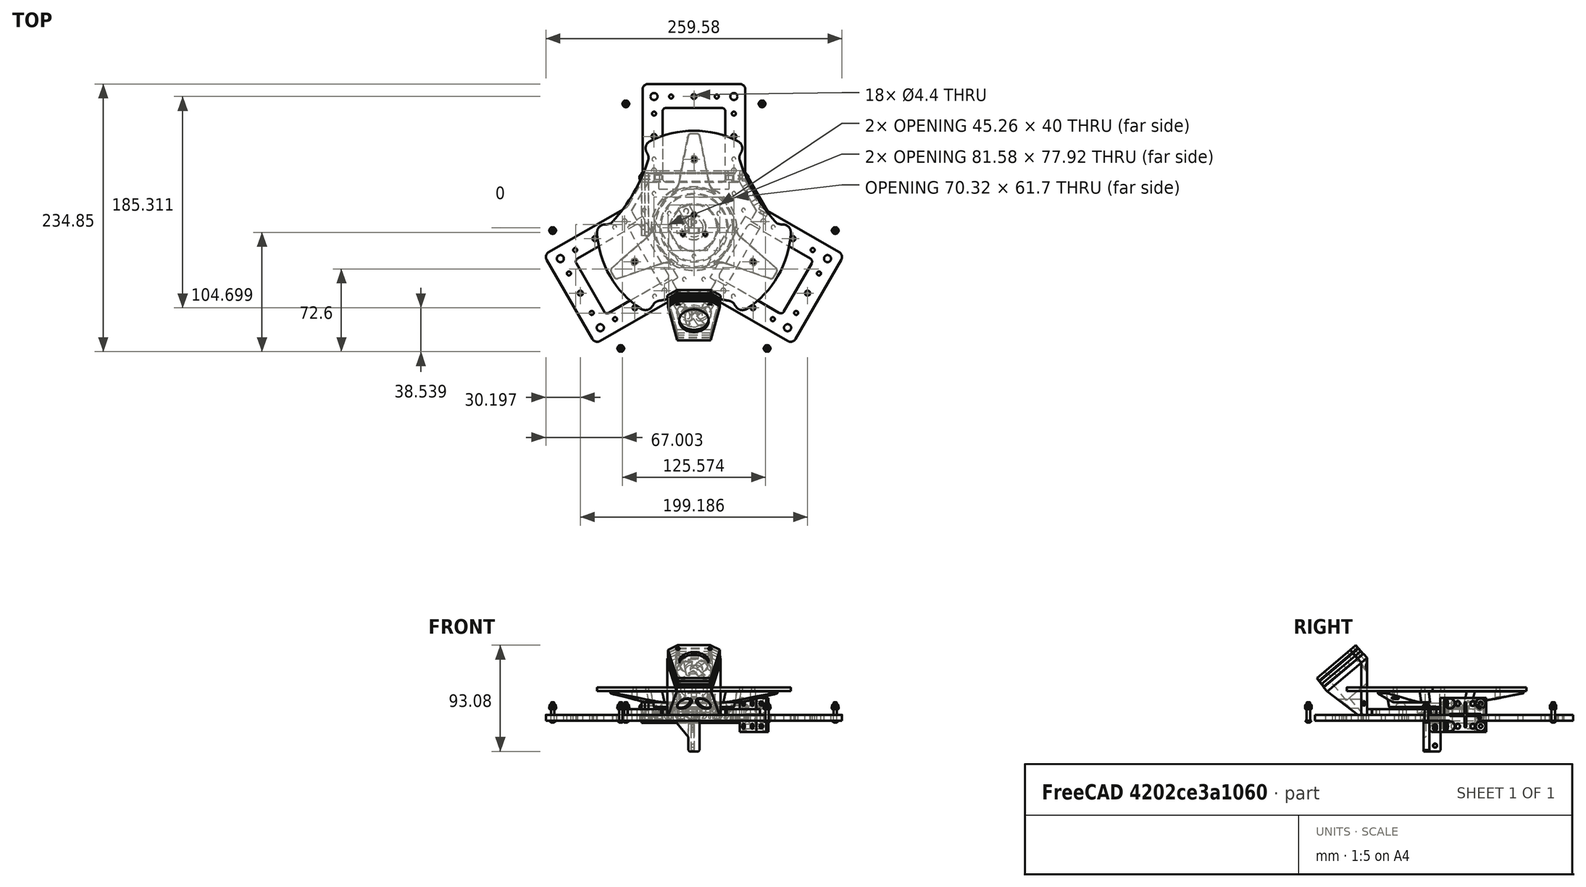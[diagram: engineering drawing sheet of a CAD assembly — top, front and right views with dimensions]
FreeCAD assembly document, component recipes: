
FREECAD ASSEMBLY — COMPONENT RECIPES ("structures")

This assembly document has 14 components, labeled P0..P13 below (a component is one placed body or linked part). 12 of them carry a construction recipe — the FreeCAD feature program that regenerates the part from scratch, quoted from this document or its linked companion documents; the rest are supplied as boundary geometry only. No exploded tour is included for this assembly.
NOTE — this tour is split across 2 documents so each fits a 32k-token context. This is document 1: the component sections continue in the remaining 1 document, each repeating the header above.
COMPONENT P0 — recipe-attached ("PlaqueIntermediaire", modeled in this document).
Construction recipe (the document's own serialized feature program — sketch geometry with constraints, then the solid features built on it; lengths are millimeters unless a unit is written):

FEATURE [Sketcher::SketchObject] Sketch043
  ArcFitTolerance = 0
  AttachmentSupport = -> [XY_Plane031]
  ExternalBSplineMaxDegree = 0
  ExternalBSplineTolerance = 0
  FullyConstrained = true
  InternalTolerance = 1e-06
  InvalidShape = false
  MakeInternals = false
  MapMode = 5
  Support = -> [XY_Plane031]
  TreeRank = 0
  ValidateShape = true
  sketch-geometry (13):
    g0: LineSegment StartX=0 StartY=0 StartZ=0 EndX=0 EndY=-54.641 EndZ=0
    g1: LineSegment StartX=0 StartY=-54.641 StartZ=0 EndX=-14.641 EndY=-54.641 EndZ=0
    g2: LineSegment StartX=-14.641 StartY=-54.641 StartZ=0 EndX=-19.641 EndY=-45.9808 EndZ=0
    g3: LineSegment StartX=-19.641 StartY=-45.9808 StartZ=0 EndX=-28.3013 EndY=-50.9808 EndZ=0
    g4: LineSegment StartX=-28.3013 StartY=-50.9808 StartZ=0 EndX=-58.3013 EndY=0.980762 EndZ=0
    g5: LineSegment StartX=-58.3013 StartY=0.980762 StartZ=0 EndX=-49.641 EndY=5.98076 EndZ=0
    g6: LineSegment StartX=-49.641 StartY=5.98076 StartZ=0 EndX=-54.641 EndY=14.641 EndZ=0
    g7: LineSegment StartX=-54.641 StartY=14.641 StartZ=0 EndX=-47.3205 EndY=27.3205 EndZ=0
    g8: LineSegment StartX=-47.3205 StartY=27.3205 StartZ=0 EndX=0 EndY=0 EndZ=0
    g9: LineSegment [constr] StartX=-49.641 StartY=5.98076 StartZ=0 EndX=-19.641 EndY=-45.9808 EndZ=0
    g10: Circle CenterX=-43.4808 CenterY=15.3109 CenterZ=0 NormalX=0 NormalY=0 NormalZ=1 AngleXU=0 Radius=1.6
    g11: Circle CenterX=-8.48076 CenterY=-45.3109 CenterZ=0 NormalX=0 NormalY=0 NormalZ=1 AngleXU=0 Radius=1.6
    g12: LineSegment [constr] StartX=0 StartY=0 StartZ=0 EndX=-43.3013 EndY=-25 EndZ=0
  constraints (35):
    c: Coincident(g0,g-1)
    c: PointOnObject(g0,g-2)
    c: Coincident(g1,g0)
    c: Horizontal(g1)
    c: Coincident(g1,g2)
    c: Coincident(g2,g3)
    c: Coincident(g3,g4)
    c: Coincident(g4,g5)
    c: Coincident(g5,g6)
    c: Coincident(g6,g7)
    c: Coincident(g7,g8)
    c: Coincident(g8,g0)
    c: Angle(g8,g0) = 2.0944
    c: Perpendicular(g7,g8)
    c: Perpendicular(g3,g2)
    c: Perpendicular(g4,g3)
    c: Perpendicular(g4,g5)
    c: Perpendicular(g6,g5)
    c: Equal(g7,g1)
    c: Coincident(g9,g5)
    c: Tangent(g9,g2) = 1.5708
    c: Equal(g2,g3)
    c: Equal(g5,g6)
    c: Distance(g6) = 10
    c: Equal(g0,g8)
    c: Distance(g4) = 60
    c: Distance(g0,g9) = 40
    c: Coincident(g12,g0)
    c: PointOnObject(g12,g4)
    c: Perpendicular(g4,g12)
    c: Symmetric(g11,g10,g12)
    c: Diameter(g10) = 3.2
    c: Equal(g10,g11)
    c: Distance(g11,g2) = 10
    c: Distance(g11,g12) = 35
FEATURE [PartDesign::Pad] Pad027
  AddSubType = 0
  AutoTaperInnerAngle = false
  CheckUpToFaceLimits = true
  ClaimChildren = false
  Direction = (1,1,1)
  Fit = 0
  FitJoin = 0
  InnerFit = 0
  InnerFitJoin = 0
  InvalidShape = false
  Length = 5
  Length2 = 100
  Linearize = true
  NewSolid = false
  Profile = -> Sketch043
  Refine = true
  Suppress = false
  TaperInnerAngle = 0
  TaperInnerAngleRev = 0
  TreeRank = 0
  Type = 0
  ValidateShape = true
  _ProfileBasedVersion = 1
FEATURE [PartDesign::PolarPattern] PolarPattern014
  AddSubType = 0
  Angle = 360
  Axis = -> Sketch043 [N_Axis]
  BaseFeature = -> Pad027
  CopyShape = false
  InvalidShape = false
  NewSolid = false
  Occurrences = 3
  OriginalSubs = -> [Pad027]
  Originals = -> [Pad027]
  ParallelTransform = true
  Refine = true
  SubTransform = true
  Suppress = false
  TreeRank = 0
  ValidateShape = true
  _Version = 2
FEATURE [Sketcher::SketchObject] Sketch044
  ArcFitTolerance = 0
  AttachmentSupport = -> [XY_Plane031]
  ExternalBSplineMaxDegree = 0
  ExternalBSplineTolerance = 0
  FullyConstrained = true
  InternalTolerance = 1e-06
  InvalidShape = false
  MakeInternals = false
  MapMode = 5
  Support = -> [XY_Plane031]
  TreeRank = 0
  ValidateShape = true
  sketch-geometry (5):
    g0: LineSegment StartX=-35.6218 StartY=8.30127 StartZ=0 EndX=-10.6218 EndY=-35 EndZ=0
    g1: LineSegment StartX=-10.6218 StartY=-35 StartZ=0 EndX=0 EndY=-35 EndZ=0
    g2: LineSegment StartX=0 StartY=-35 StartZ=0 EndX=0 EndY=0 EndZ=0
    g3: LineSegment StartX=0 StartY=0 StartZ=0 EndX=-30.3109 EndY=17.5 EndZ=0
    g4: LineSegment StartX=-30.3109 StartY=17.5 StartZ=0 EndX=-35.6218 EndY=8.30127 EndZ=0
  constraints (14):
    c: Coincident(g0,g1)
    c: PointOnObject(g1,g-2)
    c: Horizontal(g1)
    c: Coincident(g1,g2)
    c: Coincident(g2,g-1)
    c: Coincident(g2,g3)
    c: Coincident(g3,g4)
    c: Coincident(g4,g0)
    c: Perpendicular(g4,g3)
    c: Equal(g4,g1)
    c: Equal(g2,g3)
    c: Angle(g3,g2) = 2.0944
    c: Distance(g0) = 50
    c: DistanceY(g2,g2) = 35
FEATURE [PartDesign::Pocket] Pocket017
  AddSubType = 1
  AutoTaperInnerAngle = false
  BaseFeature = -> PolarPattern014
  CheckUpToFaceLimits = true
  ClaimChildren = false
  Fit = 0
  FitJoin = 0
  InnerFit = 0
  InnerFitJoin = 0
  InvalidShape = false
  Length = 5
  Length2 = 100
  Linearize = true
  NewSolid = false
  Profile = -> Sketch044
  Refine = true
  Reversed = true
  Suppress = false
  TaperInnerAngle = 0
  TaperInnerAngleRev = 0
  TreeRank = 0
  Type = 1
  ValidateShape = true
  _ProfileBasedVersion = 1
  _Version = 0
FEATURE [PartDesign::PolarPattern] PolarPattern015
  AddSubType = 0
  Angle = 360
  Axis = -> Sketch044 [N_Axis]
  BaseFeature = -> Pocket017
  CopyShape = false
  InvalidShape = false
  NewSolid = false
  Occurrences = 3
  OriginalSubs = -> [Pocket017]
  Originals = -> [Pocket017]
  ParallelTransform = true
  Refine = true
  SubTransform = true
  Suppress = false
  TreeRank = 0
  ValidateShape = true
  _Version = 2
FEATURE [PartDesign::Chamfer] Chamfer007
  AddSubType = 0
  Angle = 45
  Base = -> PolarPattern015 [Edge8,Edge66,Edge67,Edge68,Edge77,Edge78]
  BaseFeature = -> PolarPattern015
  ChamferType = 0
  FlipDirection = false
  InvalidShape = false
  NewSolid = false
  Refine = true
  Size = 1
  Size2 = 1
  SupportTransform = false
  Suppress = false
  TreeRank = 0
  ValidateShape = true
FEATURE [PartDesign::Fillet] Fillet014
  AddSubType = 0
  Base = -> Chamfer007 [Edge101,Edge103,Edge104,Edge105,Edge106,Edge102]
  BaseFeature = -> Chamfer007
  InvalidShape = false
  NewSolid = false
  Radius = 3
  Refine = true
  SupportTransform = false
  Suppress = false
  TreeRank = 0
  ValidateShape = true
FEATURE [PartDesign::Body] Body024  label="PlaqueIntermediaire"
  AutoGroupSolids = false
  ClaimAllChildren = false
  ExportMode = 0
  Group = -> [Sketch043,Pad027,PolarPattern014,Sketch044,Pocket017,PolarPattern015,Chamfer007,Fillet014]
  InvalidShape = false
  Origin = -> Origin036
  SingleSolid = true
  Tip = -> Fillet014
  TreeRank = 0
  ValidateShape = true
  _ExportChildren = -> [Pad027,PolarPattern014,Pocket017,PolarPattern015,Chamfer007,Fillet014]
  _GroupVersion = 1
COMPONENT P1 — recipe-attached ("CoinStandard", modeled in this document).
Construction recipe (the document's own serialized feature program — sketch geometry with constraints, then the solid features built on it; lengths are millimeters unless a unit is written):

FEATURE [Sketcher::SketchObject] Sketch060
  ArcFitTolerance = 0
  AttachmentSupport = -> [XY_Plane037]
  ExternalBSplineMaxDegree = 0
  ExternalBSplineTolerance = 0
  FullyConstrained = true
  InternalTolerance = 1e-06
  InvalidShape = false
  MakeInternals = false
  MapMode = 5
  Support = -> [XY_Plane037]
  TreeRank = 0
  ValidateShape = true
  sketch-geometry (10):
    g0: LineSegment [constr] StartX=0 StartY=0 StartZ=0 EndX=34.641 EndY=-20 EndZ=0
    g1: LineSegment [constr] StartX=0 StartY=0 StartZ=0 EndX=-34.641 EndY=-20 EndZ=0
    g2: LineSegment [constr] StartX=-34.641 StartY=-20 StartZ=0 EndX=-14.641 EndY=-54.641 EndZ=0
    g3: LineSegment [constr] StartX=34.641 StartY=-20 StartZ=0 EndX=14.641 EndY=-54.641 EndZ=0
    g4: LineSegment StartX=-14.641 StartY=-54.641 StartZ=0 EndX=-23.3013 EndY=-59.641 EndZ=0
    g5: LineSegment StartX=14.641 StartY=-54.641 StartZ=0 EndX=23.3013 EndY=-59.641 EndZ=0
    g6: LineSegment StartX=-23.3013 StartY=-59.641 StartZ=0 EndX=-15 EndY=-89.641 EndZ=0
    g7: LineSegment StartX=23.3013 StartY=-59.641 StartZ=0 EndX=15 EndY=-89.641 EndZ=0
    g8: LineSegment StartX=-14.641 StartY=-54.641 StartZ=0 EndX=14.641 EndY=-54.641 EndZ=0
    g9: LineSegment StartX=-15 StartY=-89.641 StartZ=0 EndX=15 EndY=-89.641 EndZ=0
  constraints (24):
    c: Coincident(g0,g-1)
    c: Coincident(g1,g0)
    c: Symmetric(g0,g1,g-2)
    c: Angle(g1,g0) = 2.0944
    c: Coincident(g2,g1)
    c: Perpendicular(g1,g2)
    c: Coincident(g3,g0)
    c: Symmetric(g3,g2,g-2)
    c: Distance(g2) = 40
    c: Distance(g0) = 40
    c: Coincident(g4,g2)
    c: Coincident(g5,g3)
    c: Perpendicular(g3,g5)
    c: Symmetric(g4,g5,g-2)
    c: Distance(g5) = 10
    c: Coincident(g6,g4)
    c: Coincident(g7,g5)
    c: Symmetric(g7,g6,g-2)
    c: DistanceY(g7,g3) = 35
    c: Coincident(g8,g4)
    c: Coincident(g8,g5)
    c: Coincident(g9,g6)
    c: Coincident(g9,g7)
    c: DistanceX(g9,g9) = 30
FEATURE [PartDesign::Pad] Pad034
  AddSubType = 0
  AutoTaperInnerAngle = false
  CheckUpToFaceLimits = true
  ClaimChildren = false
  Direction = (1,1,1)
  Fit = 0
  FitJoin = 0
  InnerFit = 0
  InnerFitJoin = 0
  InvalidShape = false
  Length = 50
  Length2 = 100
  Linearize = true
  NewSolid = false
  Profile = -> Sketch060
  Refine = true
  Suppress = false
  TaperInnerAngle = 0
  TaperInnerAngleRev = 0
  TreeRank = 0
  Type = 0
  ValidateShape = true
  _ProfileBasedVersion = 1
FEATURE [Sketcher::SketchObject] Sketch061
  ArcFitTolerance = 0
  AttachmentSupport = -> [YZ_Plane037]
  ExternalBSplineMaxDegree = 0
  ExternalBSplineTolerance = 0
  ExternalGeometry = -> [Pad034]
  FullyConstrained = true
  InternalTolerance = 1e-06
  InvalidShape = false
  MakeInternals = false
  MapMode = 5
  Placement = pos=(0,0,0) rot=(0.57735,0.57735,0.57735;2.0944rad)
  Support = -> [YZ_Plane037]
  TreeRank = 0
  ValidateShape = true
  sketch-geometry (4):
    g0: LineSegment StartX=-62.641 StartY=0 StartZ=0 EndX=-89.641 EndY=20.6315 EndZ=0
    g1: LineSegment StartX=-62.641 StartY=0 StartZ=0 EndX=-89.641 EndY=0 EndZ=0
    g2: LineSegment StartX=-89.641 StartY=0 StartZ=0 EndX=-89.641 EndY=20.6315 EndZ=0
    g3: LineSegment [constr] StartX=-89.641 StartY=20.6315 StartZ=0 EndX=-54.641 EndY=50 EndZ=0
  constraints (11):
    c: PointOnObject(g0,g-4)
    c: PointOnObject(g0,g-1)
    c: DistanceX(g0,g-3) = 3
    c: Coincident(g0,g1)
    c: PointOnObject(g1,g-4)
    c: Horizontal(g1)
    c: Coincident(g1,g2)
    c: Coincident(g2,g0)
    c: Coincident(g3,g0)
    c: Coincident(g3,g-5)
    c: Angle(g-4,g3) = 2.26893
FEATURE [PartDesign::Pocket] Pocket025
  AddSubType = 1
  AutoTaperInnerAngle = false
  BaseFeature = -> Pad034
  CheckUpToFaceLimits = true
  ClaimChildren = false
  Fit = 0
  FitJoin = 0
  InnerFit = 0
  InnerFitJoin = 0
  InvalidShape = false
  Length = 5
  Length2 = 100
  Linearize = true
  Midplane = true
  NewSolid = false
  Profile = -> Sketch061
  Refine = true
  Suppress = false
  TaperInnerAngle = 0
  TaperInnerAngleRev = 0
  TreeRank = 0
  Type = 1
  ValidateShape = true
  _ProfileBasedVersion = 1
  _Version = 1
FEATURE [Sketcher::SketchObject] Sketch062
  ArcFitTolerance = 0
  AttachmentSupport = -> [YZ_Plane037]
  ExternalBSplineMaxDegree = 0
  ExternalBSplineTolerance = 0
  ExternalGeometry = -> [Pocket025]
  FullyConstrained = true
  InternalTolerance = 1e-06
  InvalidShape = false
  MakeInternals = false
  MapMode = 5
  Placement = pos=(0,0,0) rot=(0.57735,0.57735,0.57735;2.0944rad)
  Support = -> [YZ_Plane037]
  TreeRank = 0
  ValidateShape = true
  sketch-geometry (3):
    g0: LineSegment StartX=-89.641 StartY=50 StartZ=0 EndX=-89.641 EndY=20.6315 EndZ=0
    g1: LineSegment StartX=-89.641 StartY=20.6315 StartZ=0 EndX=-54.641 EndY=50 EndZ=0
    g2: LineSegment StartX=-89.641 StartY=50 StartZ=0 EndX=-54.641 EndY=50 EndZ=0
  constraints (6):
    c: Coincident(g1,g0)
    c: Coincident(g-3,g0)
    c: Coincident(g-3,g0)
    c: Coincident(g2,g0)
    c: Coincident(g2,g1)
    c: Coincident(g1,g-5)
FEATURE [PartDesign::Pocket] Pocket026
  AddSubType = 1
  AutoTaperInnerAngle = false
  BaseFeature = -> Pocket025
  CheckUpToFaceLimits = true
  ClaimChildren = false
  Fit = 0
  FitJoin = 0
  InnerFit = 0
  InnerFitJoin = 0
  InvalidShape = false
  Length = 5
  Length2 = 100
  Linearize = true
  Midplane = true
  NewSolid = false
  Profile = -> Sketch062
  Refine = true
  Suppress = false
  TaperInnerAngle = 0
  TaperInnerAngleRev = 0
  TreeRank = 0
  Type = 1
  ValidateShape = true
  _ProfileBasedVersion = 1
  _Version = 1
FEATURE [PartDesign::Plane] DatumPlane
  AttachmentOffset = pos=(0,0,-30) rot=(0,0,1;0rad)
  AttachmentSupport = -> [Pocket026]
  InvalidShape = false
  Length = 67.9904
  MapMode = 5
  MinimumLength = 10
  MinimumWidth = 10
  Placement = pos=(-35,-60.6218,3.3e-15) rot=(0.186157,0.694747,0.694747;2.77349rad)
  ResizeMode = 0
  Support = -> [Pocket026]
  TreeRank = 0
  ValidateShape = true
  Width = 50
FEATURE [Sketcher::SketchObject] Sketch063
  ArcFitTolerance = 0
  AttachmentSupport = -> [DatumPlane]
  ExternalBSplineMaxDegree = 0
  ExternalBSplineTolerance = 0
  ExternalGeometry = -> [Pocket026]
  FullyConstrained = true
  InternalTolerance = 1e-06
  InvalidShape = false
  MakeInternals = false
  MapMode = 5
  Placement = pos=(-35,-60.6218,3.3e-15) rot=(0.186157,0.694747,0.694747;2.77349rad)
  Support = -> [DatumPlane]
  TreeRank = 0
  ValidateShape = true
  sketch-geometry (2):
    g0: Circle CenterX=-45 CenterY=10 CenterZ=0 NormalX=0 NormalY=0 NormalZ=1 AngleXU=0 Radius=1.6
    g1: LineSegment [constr] StartX=-50 StartY=10 StartZ=0 EndX=-40 EndY=10 EndZ=0
  constraints (6):
    c: PointOnObject(g1,g-3)
    c: PointOnObject(g1,g-4)
    c: Horizontal(g1)
    c: Symmetric(g1,g1,g0)
    c: Diameter(g0) = 3.2
    c: Distance(g-3,g1) = 10
FEATURE [PartDesign::Hole] Hole001
  AddSubType = 1
  BaseFeature = -> Pocket026
  ClaimChildren = false
  CustomThreadClearance = 0
  Depth = 39
  DepthType = 0
  Diameter = 3.2
  DrillForDepth = false
  DrillPoint = 1
  DrillPointAngle = 118
  Fit = 0
  FitJoin = 0
  HoleCutCountersinkAngle = 90
  HoleCutCustomValues = true
  HoleCutDepth = 27
  HoleCutDiameter = 8
  HoleCutType = 1
  InnerFit = 0
  InnerFitJoin = 0
  InvalidShape = false
  ModelThread = false
  NewSolid = false
  Profile = -> Sketch063
  Refine = true
  Reversed = true
  Suppress = false
  Tapered = false
  TaperedAngle = 90
  ThreadClass = 0
  ThreadDepth = 39
  ThreadDepthType = 0
  ThreadDirection = 0
  ThreadFit = 0
  ThreadSize = 0
  ThreadType = 0
  Threaded = false
  TreeRank = 0
  UseCustomThreadClearance = false
  ValidateShape = true
  _ProfileBasedVersion = 1
FEATURE [PartDesign::Mirrored] Mirrored006
  AddSubType = 0
  BaseFeature = -> Hole001
  CopyShape = false
  InvalidShape = false
  MirrorPlane = -> YZ_Plane037
  NewSolid = false
  OriginalSubs = -> [Hole001]
  Originals = -> [Hole001]
  ParallelTransform = true
  Refine = true
  SubTransform = true
  Suppress = false
  TreeRank = 0
  ValidateShape = true
  _Version = 3
FEATURE [Sketcher::SketchObject] Sketch064
  ArcFitTolerance = 0
  AttachmentSupport = -> [Mirrored006]
  ExternalBSplineMaxDegree = 0
  ExternalBSplineTolerance = 0
  ExternalGeometry = -> [Mirrored006]
  FullyConstrained = true
  InternalTolerance = 1e-06
  InvalidShape = false
  MakeInternals = false
  MapMode = 5
  Placement = pos=(-2.64e-14,-47.1965,56.2467) rot=(1,0,0;0.698132rad)
  Support = -> [Mirrored006]
  TreeRank = 0
  ValidateShape = true
  sketch-geometry (2):
    g0: Circle CenterX=-14 CenterY=-14.7181 CenterZ=0 NormalX=0 NormalY=0 NormalZ=1 AngleXU=0 Radius=2.05
    g1: Circle CenterX=14 CenterY=-14.7181 CenterZ=0 NormalX=0 NormalY=0 NormalZ=1 AngleXU=0 Radius=2.05
  constraints (5):
    c: Symmetric(g1,g0,g-2)
    c: Diameter(g0) = 4.1
    c: Equal(g0,g1)
    c: DistanceX(g0,g1) = 28
    c: DistanceY(g0,g-3) = 5
FEATURE [PartDesign::Pocket] Pocket027
  AddSubType = 1
  AutoTaperInnerAngle = false
  BaseFeature = -> Mirrored006
  CheckUpToFaceLimits = true
  ClaimChildren = false
  Fit = 0
  FitJoin = 0
  InnerFit = 0
  InnerFitJoin = 0
  InvalidShape = false
  Length = 5
  Length2 = 100
  Linearize = true
  NewSolid = false
  Profile = -> Sketch064
  Refine = true
  Suppress = false
  TaperInnerAngle = 0
  TaperInnerAngleRev = 0
  TreeRank = 0
  Type = 1
  ValidateShape = true
  _ProfileBasedVersion = 1
  _Version = 1
FEATURE [Sketcher::SketchObject] Sketch065
  ArcFitTolerance = 0
  AttachmentSupport = -> [Pocket027]
  ExternalBSplineMaxDegree = 0
  ExternalBSplineTolerance = 0
  ExternalGeometry = -> [Pocket027]
  FullyConstrained = true
  InternalTolerance = 1e-06
  InvalidShape = false
  MakeInternals = false
  MapMode = 5
  Placement = pos=(-2.64e-14,-47.1965,56.2467) rot=(1,0,0;0.698132rad)
  Support = -> [Pocket027]
  TreeRank = 0
  ValidateShape = true
  sketch-geometry (3):
    g0: Circle CenterX=0 CenterY=-32.5627 CenterZ=0 NormalX=0 NormalY=0 NormalZ=1 AngleXU=0 Radius=15
    g1: GeomPoint [constr] X=2e-16 Y=-55.4073 Z=0
    g2: GeomPoint [constr] X=0 Y=-9.71807 Z=0
  constraints (6):
    c: PointOnObject(g0,g-2)
    c: Diameter(g0) = 30
    c: PointOnObject(g2,g-2)
    c: PointOnObject(g2,g-3)
    c: PointOnObject(g1,g-4)
    c: Symmetric(g1,g2,g0)
FEATURE [PartDesign::Pocket] Pocket028
  AddSubType = 1
  AutoTaperInnerAngle = false
  BaseFeature = -> Pocket027
  CheckUpToFaceLimits = true
  ClaimChildren = false
  Fit = 0
  FitJoin = 0
  InnerFit = 0
  InnerFitJoin = 0
  InvalidShape = false
  Length = 17
  Length2 = 100
  Linearize = true
  NewSolid = false
  Profile = -> Sketch065
  Refine = true
  Suppress = false
  TaperInnerAngle = 0
  TaperInnerAngleRev = 0
  TreeRank = 0
  Type = 0
  ValidateShape = true
  _ProfileBasedVersion = 1
  _Version = 1
FEATURE [Sketcher::SketchObject] Sketch066
  ArcFitTolerance = 0
  AttachmentSupport = -> [Pocket028]
  ExternalBSplineMaxDegree = 0
  ExternalBSplineTolerance = 0
  ExternalGeometry = -> [Pocket028]
  FullyConstrained = true
  InternalTolerance = 1e-06
  InvalidShape = false
  MakeInternals = false
  MapMode = 5
  Placement = pos=(-2.64e-14,-47.1965,56.2467) rot=(1,0,0;0.698132rad)
  Support = -> [Pocket028]
  TreeRank = 0
  ValidateShape = true
  sketch-geometry (4):
    g0: ArcOfCircle CenterX=0 CenterY=-32.5627 CenterZ=0 NormalX=0 NormalY=0 NormalZ=1 AngleXU=0 Radius=11.5 StartAngle=3.22982 EndAngle=6.19496
    g1: LineSegment StartX=-11.4553 StartY=-33.576 StartZ=0 EndX=-12.3039 EndY=-23.9828 EndZ=0
    g2: LineSegment StartX=12.3039 StartY=-23.9828 StartZ=0 EndX=11.4553 EndY=-33.576 EndZ=0
    g3: LineSegment StartX=-12.3039 StartY=-23.9828 StartZ=0 EndX=12.3039 EndY=-23.9828 EndZ=0
  constraints (8):
    c: Coincident(g0,g-3)
    c: Diameter(g0) = 23
    c: Coincident(g1,g-4)
    c: Coincident(g2,g-4)
    c: Coincident(g3,g1)
    c: Coincident(g3,g2)
    c: Tangent(g1,g0) = 1.5708
    c: Tangent(g2,g0) = 1.5708
FEATURE [PartDesign::Pocket] Pocket029
  AddSubType = 1
  AutoTaperInnerAngle = false
  BaseFeature = -> Pocket028
  CheckUpToFaceLimits = true
  ClaimChildren = false
  Fit = 0
  FitJoin = 0
  InnerFit = 0
  InnerFitJoin = 0
  InvalidShape = false
  Length = 5
  Length2 = 100
  Linearize = true
  NewSolid = false
  Profile = -> Sketch066
  Refine = true
  Suppress = false
  TaperInnerAngle = 0
  TaperInnerAngleRev = 0
  TreeRank = 0
  Type = 1
  ValidateShape = true
  _ProfileBasedVersion = 1
  _Version = 1
FEATURE [PartDesign::Chamfer] Chamfer018
  AddSubType = 0
  Angle = 45
  Base = -> Pocket029 [Edge44,Edge31]
  BaseFeature = -> Pocket029
  ChamferType = 0
  FlipDirection = false
  InvalidShape = false
  NewSolid = false
  Refine = true
  Size = 0.4
  Size2 = 1
  SupportTransform = false
  Suppress = false
  TreeRank = 0
  ValidateShape = true
FEATURE [PartDesign::Pad] Pad036
  AddSubType = 0
  AutoTaperInnerAngle = false
  BaseFeature = -> Chamfer018
  CheckUpToFaceLimits = true
  ClaimChildren = false
  Direction = (1,1,1)
  Fit = 0
  FitJoin = 0
  InnerFit = 0
  InnerFitJoin = 0
  InvalidShape = false
  Length = 5
  Length2 = 100
  Linearize = true
  NewSolid = false
  Profile = -> Chamfer018 [Face5]
  Refine = true
  Suppress = false
  TaperInnerAngle = 0
  TaperInnerAngleRev = 0
  TreeRank = 0
  Type = 0
  ValidateShape = true
  _ProfileBasedVersion = 1
FEATURE [PartDesign::Chamfer] Chamfer022
  AddSubType = 0
  Angle = 45
  Base = -> Pad036 [Face15]
  BaseFeature = -> Pad036
  ChamferType = 0
  FlipDirection = false
  InvalidShape = false
  NewSolid = false
  Refine = true
  Size = 0.4
  Size2 = 1
  SupportTransform = false
  Suppress = false
  TreeRank = 0
  ValidateShape = true
FEATURE [PartDesign::Chamfer] Chamfer023
  AddSubType = 0
  Angle = 45
  Base = -> Chamfer022 [Edge64,Edge63]
  BaseFeature = -> Chamfer022
  ChamferType = 0
  FlipDirection = false
  InvalidShape = false
  NewSolid = false
  Refine = true
  Size = 1
  Size2 = 1
  SupportTransform = false
  Suppress = false
  TreeRank = 0
  ValidateShape = true
FEATURE [PartDesign::Body] Body029  label="CoinStandard"
  AutoGroupSolids = false
  ClaimAllChildren = false
  ExportMode = 0
  Group = -> [Sketch060,Pad034,Sketch061,Pocket025,Sketch062,Pocket026,DatumPlane,Sketch063,Hole001,Mirrored006,Sketch064,Pocket027,Sketch065,Pocket028,Sketch066,Pocket029,Chamfer018,Pad036,Chamfer022,Chamfer023]
  InvalidShape = false
  Origin = -> Origin046
  SingleSolid = true
  Tip = -> Chamfer023
  TreeRank = 0
  ValidateShape = true
  _ExportChildren = -> [Pad034,Pocket025,Pocket026,DatumPlane,Hole001,Mirrored006,Pocket027,Pocket028,Pocket029,Chamfer018,Pad036,Chamfer022,Chamfer023]
  _GroupVersion = 1
COMPONENT P2 — recipe-attached ("Link075(Semelle)", modeled in this document).
Construction recipe (the document's own serialized feature program — sketch geometry with constraints, then the solid features built on it; lengths are millimeters unless a unit is written):

FEATURE [Sketcher::SketchObject] Sketch032
  ArcFitTolerance = 0
  AttachmentSupport = -> [XY_Plane026]
  ExternalBSplineMaxDegree = 0
  ExternalBSplineTolerance = 0
  FullyConstrained = true
  InternalTolerance = 1e-06
  InvalidShape = false
  MakeInternals = false
  MapMode = 5
  Support = -> [XY_Plane026]
  TreeRank = 0
  ValidateShape = true
  sketch-geometry (56):
    g0: LineSegment StartX=-131.619 StartY=-24.0289 StartZ=0 EndX=-58.007 EndY=18.4711 EndZ=0
    g1: LineSegment StartX=-58.007 StartY=18.4711 StartZ=0 EndX=-45 EndY=41 EndZ=0
    g2: LineSegment StartX=-45 StartY=41 StartZ=0 EndX=-45 EndY=126 EndZ=0
    g3: LineSegment StartX=-45 StartY=126 StartZ=0 EndX=45 EndY=126 EndZ=0
    g4: LineSegment StartX=45 StartY=126 StartZ=0 EndX=45 EndY=41 EndZ=0
    g5: LineSegment StartX=45 StartY=41 StartZ=0 EndX=58.007 EndY=18.4711 EndZ=0
    g6: LineSegment StartX=58.007 StartY=18.4711 StartZ=0 EndX=131.619 EndY=-24.0289 EndZ=0
    g7: LineSegment StartX=131.619 StartY=-24.0289 StartZ=0 EndX=86.6192 EndY=-101.971 EndZ=0
    g8: LineSegment StartX=86.6192 StartY=-101.971 StartZ=0 EndX=13.007 EndY=-59.4711 EndZ=0
    g9: LineSegment StartX=13.007 StartY=-59.4711 StartZ=0 EndX=-13.007 EndY=-59.4711 EndZ=0
    g10: LineSegment StartX=-13.007 StartY=-59.4711 StartZ=0 EndX=-86.6192 EndY=-101.971 EndZ=0
    g11: LineSegment StartX=-86.6192 StartY=-101.971 StartZ=0 EndX=-131.619 EndY=-24.0289 EndZ=0
    g12: LineSegment [constr] StartX=-1e-16 StartY=1e-16 StartZ=0 EndX=-1e-16 EndY=126 EndZ=0
    g13: LineSegment [constr] StartX=-1e-16 StartY=1e-16 StartZ=0 EndX=-109.119 EndY=-63 EndZ=0
    g14: LineSegment [constr] StartX=-1e-16 StartY=1e-16 StartZ=0 EndX=109.119 EndY=-63 EndZ=0
    g15: LineSegment StartX=-27.5 StartY=40 StartZ=0 EndX=27.5 EndY=40 EndZ=0
    g16: LineSegment StartX=27.5 StartY=40 StartZ=0 EndX=27.5 EndY=105 EndZ=0
    g17: LineSegment StartX=27.5 StartY=105 StartZ=0 EndX=-27.5 EndY=105 EndZ=0
    g18: LineSegment StartX=-27.5 StartY=105 StartZ=0 EndX=-27.5 EndY=40 EndZ=0
    g19: LineSegment StartX=20.891 StartY=-43.8157 StartZ=0 EndX=48.391 EndY=3.8157 EndZ=0
    g20: LineSegment StartX=48.391 StartY=3.8157 StartZ=0 EndX=104.683 EndY=-28.6843 EndZ=0
    g21: LineSegment StartX=104.683 StartY=-28.6843 StartZ=0 EndX=77.1827 EndY=-76.3157 EndZ=0
    g22: LineSegment StartX=77.1827 StartY=-76.3157 StartZ=0 EndX=20.891 EndY=-43.8157 EndZ=0
    g23: LineSegment StartX=-104.683 StartY=-28.6843 StartZ=0 EndX=-77.1827 EndY=-76.3157 EndZ=0
    g24: LineSegment StartX=-77.1827 StartY=-76.3157 StartZ=0 EndX=-20.891 EndY=-43.8157 EndZ=0
    g25: LineSegment StartX=-20.891 StartY=-43.8157 StartZ=0 EndX=-48.391 EndY=3.8157 EndZ=0
    g26: LineSegment StartX=-48.391 StartY=3.8157 StartZ=0 EndX=-104.683 EndY=-28.6843 EndZ=0
    g27: Circle [constr] CenterX=-1e-16 CenterY=1e-16 CenterZ=0 NormalX=0 NormalY=0 NormalZ=1 AngleXU=0 Radius=48.5412
    g28: LineSegment StartX=-11.547 StartY=-20 StartZ=0 EndX=-23.094 EndY=0 EndZ=0
    g29: LineSegment StartX=-23.094 StartY=-1.3e-15 StartZ=0 EndX=-11.547 EndY=20 EndZ=0
    g30: LineSegment StartX=-11.547 StartY=20 StartZ=0 EndX=11.547 EndY=20 EndZ=0
    g31: LineSegment StartX=11.547 StartY=20 StartZ=0 EndX=23.094 EndY=0 EndZ=0
    g32: LineSegment StartX=23.094 StartY=9e-16 StartZ=0 EndX=11.547 EndY=-20 EndZ=0
    g33: LineSegment StartX=11.547 StartY=-20 StartZ=0 EndX=-11.547 EndY=-20 EndZ=0
    g34: Circle [constr] CenterX=-1e-16 CenterY=1e-16 CenterZ=0 NormalX=0 NormalY=0 NormalZ=1 AngleXU=0 Radius=23.094
    g35: Circle CenterX=-21.6506 CenterY=12.5 CenterZ=0 NormalX=0 NormalY=0 NormalZ=1 AngleXU=0 Radius=1.6
    g36: Circle CenterX=21.6506 CenterY=12.5 CenterZ=0 NormalX=0 NormalY=0 NormalZ=1 AngleXU=0 Radius=1.6
    g37: Circle CenterX=0 CenterY=-25 CenterZ=0 NormalX=0 NormalY=0 NormalZ=1 AngleXU=0 Radius=1.6
    g38: LineSegment [constr] StartX=0 StartY=-25 StartZ=0 EndX=-1e-16 EndY=0 EndZ=0
    g39: LineSegment [constr] StartX=-1e-16 StartY=1e-16 StartZ=0 EndX=21.6506 EndY=12.5 EndZ=0
    g40: LineSegment [constr] StartX=-1e-16 StartY=1e-16 StartZ=0 EndX=-21.6506 EndY=12.5 EndZ=0
    g41: LineSegment [constr] StartX=-45 StartY=126 StartZ=0 EndX=-131.619 EndY=-24.0289 EndZ=0
    g42: LineSegment [constr] StartX=-86.6192 StartY=-101.971 StartZ=0 EndX=86.6192 EndY=-101.971 EndZ=0
    g43: LineSegment [constr] StartX=131.619 StartY=-24.0289 StartZ=0 EndX=45 EndY=126 EndZ=0
    g44: LineSegment [constr] StartX=-45 StartY=126 StartZ=0 EndX=-55 EndY=108.679 EndZ=0
    g45: LineSegment [constr] StartX=-55 StartY=108.679 StartZ=0 EndX=-45 EndY=41 EndZ=0
    g46: LineSegment [constr] StartX=-58.007 StartY=18.4711 StartZ=0 EndX=-121.619 EndY=-6.70835 EndZ=0
    g47: LineSegment [constr] StartX=-121.619 StartY=-6.70835 StartZ=0 EndX=-131.619 EndY=-24.0289 EndZ=0
    g48: LineSegment [constr] StartX=-86.6192 StartY=-101.971 StartZ=0 EndX=-66.6192 EndY=-101.971 EndZ=0
    g49: LineSegment [constr] StartX=-66.6192 StartY=-101.971 StartZ=0 EndX=-13.007 EndY=-59.4711 EndZ=0
    g50: LineSegment [constr] StartX=13.007 StartY=-59.4711 StartZ=0 EndX=66.6192 EndY=-101.971 EndZ=0
    g51: LineSegment [constr] StartX=66.6192 StartY=-101.971 StartZ=0 EndX=86.6192 EndY=-101.971 EndZ=0
    g52: LineSegment [constr] StartX=131.619 StartY=-24.0289 StartZ=0 EndX=121.619 EndY=-6.70835 EndZ=0
    g53: LineSegment [constr] StartX=121.619 StartY=-6.70835 StartZ=0 EndX=58.007 EndY=18.4711 EndZ=0
    g54: LineSegment [constr] StartX=45 StartY=41 StartZ=0 EndX=55 EndY=108.679 EndZ=0
    g55: LineSegment [constr] StartX=55 StartY=108.679 StartZ=0 EndX=45 EndY=126 EndZ=0
  constraints (151):
    c: Coincident(g0,g1)
    c: Coincident(g1,g2)
    c: Vertical(g2)
    c: Coincident(g2,g3)
    c: Horizontal(g3)
    c: Coincident(g3,g4)
    c: Vertical(g4)
    c: Coincident(g4,g5)
    c: Coincident(g5,g6)
    c: Coincident(g6,g7)
    c: Coincident(g7,g8)
    c: Coincident(g8,g9)
    c: Horizontal(g9)
    c: Coincident(g9,g10)
    c: Coincident(g10,g11)
    c: Coincident(g11,g0)
    c: Parallel(g8,g6)
    c: Parallel(g10,g0)
    c: Equal(g4,g6)
    c: Equal(g6,g8)
    c: Equal(g8,g10)
    c: Equal(g10,g0)
    c: Equal(g0,g2)
    c: Perpendicular(g6,g7)
    c: Perpendicular(g11,g10)
    c: Coincident(g12,g-1)
    c: PointOnObject(g12,g3)
    c: Vertical(g12)
    c: Coincident(g13,g12)
    c: Coincident(g14,g12)
    c: Symmetric(g6,g7,g14)
    c: Symmetric(g10,g0,g13)
    c: Perpendicular(g13,g11)
    c: Perpendicular(g7,g14)
    c: DistanceX(g3,g3) = 90
    c: Equal(g9,g5)
    c: Equal(g5,g1)
    c: Angle(g14,g12) = 2.0944
    c: Angle(g12,g13) = 2.0944
    c: DistanceY(g12,g2) = 126
    c: DistanceX(g9,g9) = 26.0141
    c: Coincident(g15,g16)
    c: Coincident(g16,g17)
    c: Coincident(g17,g18)
    c: Coincident(g18,g15)
    c: Horizontal(g15)
    c: Vertical(g16)
    c: Vertical(g18)
    c: Symmetric(g16,g17,g12)
    c: DistanceX(g17,g17) = 55
    c: DistanceY(g16,g16) = 65
    c: Coincident(g19,g20)
    c: Coincident(g20,g21)
    c: Coincident(g21,g22)
    c: Coincident(g22,g19)
    c: Coincident(g23,g24)
    c: Coincident(g24,g25)
    c: Coincident(g25,g26)
    c: Coincident(g26,g23)
    c: Equal(g25,g23)
    c: Equal(g23,g19)
    c: Equal(g19,g21)
    c: Equal(g21,g15)
    c: Equal(g22,g20)
    c: Equal(g20,g16)
    c: Equal(g16,g26)
    c: Equal(g26,g24)
    c: Parallel(g24,g13)
    c: Parallel(g22,g14)
    c: Symmetric(g23,g23,g13)
    c: Symmetric(g21,g20,g14)
    c: Coincident(g27,g12)
    c: PointOnObject(g19,g27)
    c: PointOnObject(g24,g27)
    c: PointOnObject(g15,g27)
    c: Equal(g11,g7)
    c: Equal(g7,g3)
    c: Coincident(g28,g29)
    c: Coincident(g29,g30)
    c: Coincident(g30,g31)
    c: Coincident(g31,g32)
    c: Coincident(g32,g33)
    c: Coincident(g33,g28)
    c: Horizontal(g33)
    c: Horizontal(g30)
    c: Equal(g29,g30)
    c: Equal(g30,g31)
    c: Equal(g31,g32)
    c: Equal(g32,g33)
    c: Equal(g33,g28)
    c: Coincident(g34,g12)
    c: PointOnObject(g30,g34)
    c: PointOnObject(g31,g34)
    c: PointOnObject(g32,g34)
    c: PointOnObject(g28,g34)
    c: PointOnObject(g28,g34)
    c: DistanceY(g12,g30) = 20
    c: PointOnObject(g37,g-2)
    c: Equal(g37,g36)
    c: Equal(g36,g35)
    c: Diameter(g35) = 3.2
    c: Coincident(g38,g37)
    c: Coincident(g38,g12)
    c: Coincident(g39,g12)
    c: Coincident(g39,g36)
    c: Coincident(g40,g12)
    c: Coincident(g40,g35)
    c: Perpendicular(g29,g40)
    c: Perpendicular(g31,g39)
    c: Equal(g40,g38)
    c: Equal(g38,g39)
    c: DistanceY(g38,g38) = 25
    c: Coincident(g41,g3)
    c: Coincident(g41,g11)
    c: Coincident(g42,g11)
    c: Coincident(g42,g7)
    c: Coincident(g43,g7)
    c: Coincident(g43,g3)
    c: Coincident(g3,g44)
    c: PointOnObject(g44,g41)
    c: Coincident(g44,g45)
    c: Coincident(g45,g1)
    c: Coincident(g1,g46)
    c: PointOnObject(g46,g41)
    c: Coincident(g46,g47)
    c: Coincident(g47,g11)
    c: Coincident(g11,g48)
    c: Horizontal(g48)
    c: Coincident(g48,g49)
    c: Coincident(g49,g9)
    c: Coincident(g9,g50)
    c: PointOnObject(g50,g42)
    c: Coincident(g50,g51)
    c: Coincident(g51,g7)
    c: Coincident(g7,g52)
    c: PointOnObject(g52,g43)
    c: Coincident(g52,g53)
    c: Coincident(g53,g5)
    c: Coincident(g5,g54)
    c: PointOnObject(g54,g43)
    c: Coincident(g54,g55)
    c: Coincident(g55,g3)
    c: Equal(g55,g44)
    c: Equal(g44,g47)
    c: Equal(g47,g48)
    c: Equal(g48,g51)
    c: Equal(g55,g52)
    c: DistanceX(g48,g48) = 20
    c: DistanceY(g16) = 105
    c: DistanceY(g50,g12) = 101.971
    c: DistanceY(g4,g4) = 85
FEATURE [PartDesign::Pad] Pad020
  AddSubType = 0
  AutoTaperInnerAngle = false
  CheckUpToFaceLimits = true
  ClaimChildren = false
  Direction = (0,0,1)
  Fit = 0
  FitJoin = 0
  InnerFit = 0
  InnerFitJoin = 0
  InvalidShape = false
  Length = 5
  Length2 = 100
  Linearize = true
  NewSolid = false
  Profile = -> Sketch032
  Refine = true
  Reversed = true
  Suppress = false
  TaperInnerAngle = 0
  TaperInnerAngleRev = 0
  TreeRank = 0
  Type = 0
  ValidateShape = true
  _ProfileBasedVersion = 1
FEATURE [PartDesign::Fillet] Fillet008
  AddSubType = 0
  Base = -> Pad020 [Edge41,Edge44,Edge37,Edge38,Edge65,Edge62,Edge61,Edge68,Edge49,Edge50,Edge53,Edge56]
  BaseFeature = -> Pad020
  InvalidShape = false
  NewSolid = false
  Radius = 3
  Refine = true
  SupportTransform = false
  Suppress = false
  TreeRank = 0
  ValidateShape = true
FEATURE [PartDesign::Fillet] Fillet009
  AddSubType = 0
  Base = -> Fillet008 [Edge110,Edge99,Edge107,Edge106,Edge102,Edge103]
  BaseFeature = -> Fillet008
  InvalidShape = false
  NewSolid = false
  Radius = 5
  Refine = true
  SupportTransform = false
  Suppress = false
  TreeRank = 0
  ValidateShape = true
FEATURE [PartDesign::Fillet] Fillet010
  AddSubType = 0
  Base = -> Fillet009 [Edge53,Edge57,Edge67,Edge71,Edge77,Edge81]
  BaseFeature = -> Fillet009
  InvalidShape = false
  NewSolid = false
  Radius = 5
  Refine = true
  SupportTransform = false
  Suppress = false
  TreeRank = 0
  ValidateShape = true
FEATURE [Sketcher::SketchObject] Sketch033
  ArcFitTolerance = 0
  AttachmentSupport = -> [XY_Plane026]
  ExternalBSplineMaxDegree = 0
  ExternalBSplineTolerance = 0
  FullyConstrained = true
  InternalTolerance = 1e-06
  InvalidShape = false
  MakeInternals = false
  MapMode = 5
  Support = -> [XY_Plane026]
  TreeRank = 0
  ValidateShape = true
  sketch-geometry (13):
    g0: Circle CenterX=-20 CenterY=115 CenterZ=0 NormalX=0 NormalY=0 NormalZ=1 AngleXU=0 Radius=1.75
    g1: Circle CenterX=20 CenterY=115 CenterZ=0 NormalX=0 NormalY=0 NormalZ=1 AngleXU=0 Radius=1.75
    g2: Circle CenterX=-35 CenterY=60 CenterZ=0 NormalX=0 NormalY=0 NormalZ=1 AngleXU=0 Radius=1.75
    g3: Circle CenterX=-35 CenterY=100 CenterZ=0 NormalX=0 NormalY=0 NormalZ=1 AngleXU=0 Radius=1.75
    g4: Circle CenterX=35 CenterY=100 CenterZ=0 NormalX=0 NormalY=0 NormalZ=1 AngleXU=0 Radius=1.75
    g5: Circle CenterX=35 CenterY=60 CenterZ=0 NormalX=0 NormalY=0 NormalZ=1 AngleXU=0 Radius=1.75
    g6: Circle CenterX=-35 CenterY=115 CenterZ=0 NormalX=0 NormalY=0 NormalZ=1 AngleXU=0 Radius=3.1
    g7: Circle CenterX=35 CenterY=115 CenterZ=0 NormalX=0 NormalY=0 NormalZ=1 AngleXU=0 Radius=3.1
    g8: Circle CenterX=-35 CenterY=80 CenterZ=0 NormalX=0 NormalY=0 NormalZ=1 AngleXU=0 Radius=2.2
    g9: Circle CenterX=35 CenterY=80 CenterZ=0 NormalX=0 NormalY=0 NormalZ=1 AngleXU=0 Radius=2.2
    g10: Circle CenterX=-35 CenterY=50 CenterZ=0 NormalX=0 NormalY=0 NormalZ=1 AngleXU=0 Radius=2.2
    g11: Circle CenterX=35 CenterY=50 CenterZ=0 NormalX=0 NormalY=0 NormalZ=1 AngleXU=0 Radius=2.2
    g12: Circle CenterX=-1.0206e-12 CenterY=115 CenterZ=0 NormalX=0 NormalY=0 NormalZ=1 AngleXU=0 Radius=2.2
  constraints (31):
    c: Equal(g0,g3)
    c: Equal(g3,g2)
    c: Equal(g2,g1)
    c: Equal(g1,g4)
    c: Equal(g4,g5)
    c: Diameter(g0) = 3.5
    c: Symmetric(g1,g0,g-2)
    c: Symmetric(g3,g4,g-2)
    c: Symmetric(g2,g5,g-2)
    c: Vertical(g3,g2)
    c: DistanceX(g3,g4) = 70
    c: DistanceX(g0,g1) = 40
    c: DistanceY(g4,g1) = 15
    c: DistanceY(g5,g4) = 40
    c: DistanceY(g-1,g1) = 115
    c: Symmetric(g7,g6,g-2)
    c: Horizontal(g6,g0)
    c: Diameter(g7) = 6.2
    c: Equal(g7,g6)
    c: Vertical(g7,g4)
    c: Equal(g9,g8)
    c: Symmetric(g8,g9,g-2)
    c: Symmetric(g5,g4,g9)
    c: Diameter(g9) = 4.4
    c: Symmetric(g1,g0,g12)
    c: Equal(g12,g11)
    c: Equal(g11,g10)
    c: Equal(g10,g9)
    c: Vertical(g11,g5)
    c: Symmetric(g11,g10,g-2)
    c: DistanceY(g11,g5) = 10
FEATURE [PartDesign::Pocket] Pocket012
  AddSubType = 1
  AutoTaperInnerAngle = false
  BaseFeature = -> Fillet010
  CheckUpToFaceLimits = true
  ClaimChildren = false
  Fit = 0
  FitJoin = 0
  InnerFit = 0
  InnerFitJoin = 0
  InvalidShape = false
  Length = 5
  Length2 = 100
  Linearize = true
  NewSolid = false
  Profile = -> Sketch033
  Refine = true
  Suppress = false
  TaperInnerAngle = 0
  TaperInnerAngleRev = 0
  TreeRank = 0
  Type = 1
  ValidateShape = true
  _ProfileBasedVersion = 1
  _Version = 0
FEATURE [PartDesign::PolarPattern] PolarPattern013
  AddSubType = 0
  Angle = 360
  Axis = -> Sketch033 [N_Axis]
  BaseFeature = -> Pocket012
  CopyShape = false
  InvalidShape = false
  NewSolid = false
  Occurrences = 3
  OriginalSubs = -> [Pocket012]
  Originals = -> [Pocket012]
  ParallelTransform = true
  Refine = true
  SubTransform = true
  Suppress = false
  TreeRank = 0
  ValidateShape = true
  _Version = 0
FEATURE [PartDesign::Fillet] Fillet011
  AddSubType = 0
  Base = -> PolarPattern013 [Edge190,Edge189,Edge192,Edge196,Edge198,Edge194]
  BaseFeature = -> PolarPattern013
  InvalidShape = false
  NewSolid = false
  Radius = 3
  Refine = true
  SupportTransform = false
  Suppress = false
  TreeRank = 0
  ValidateShape = true
FEATURE [PartDesign::Body] Body019  label="Semelle"
  AutoGroupSolids = false
  ClaimAllChildren = false
  ExportMode = 0
  Group = -> [Sketch032,Pad020,Fillet008,Fillet009,Fillet010,Sketch033,Pocket012,PolarPattern013,Fillet011]
  InvalidShape = false
  Origin = -> Origin029
  SingleSolid = true
  Tip = -> Fillet011
  TreeRank = 0
  ValidateShape = true
  _ExportChildren = -> [Pad020,Fillet008,Fillet009,Fillet010,Pocket012,PolarPattern013,Fillet011]
  _GroupVersion = 1
COMPONENT P3 — recipe-attached ("Poignee", modeled in this document).
Construction recipe (the document's own serialized feature program — sketch geometry with constraints, then the solid features built on it; lengths are millimeters unless a unit is written):

FEATURE [Part::Part2DObjectPython] ShapeString  # Draft 2D object (typed FeaturePython)
  FontFile = <userpath>/Downloads/baveuse/baveuse.ttf
  InvalidShape = false
  Placement = pos=(-35.5,-8,-3) rot=(1,0,0;1.5708rad)
  Size = 5
  String = KARIBOUS
  Tracking = 0
  TreeRank = 0
  ValidateShape = true
FEATURE [Sketcher::SketchObject] Sketch
  ArcFitTolerance = 0
  AttachmentSupport = -> [XZ_Plane]
  ExternalBSplineMaxDegree = 0
  ExternalBSplineTolerance = 0
  FullyConstrained = true
  InternalTolerance = 1e-06
  InvalidShape = false
  MakeInternals = false
  MapMode = 5
  Placement = pos=(0,0,0) rot=(1,0,0;1.5708rad)
  Support = -> [XZ_Plane]
  TreeRank = 0
  ValidateShape = true
  sketch-geometry (4):
    g0: LineSegment StartX=-40 StartY=11 StartZ=0 EndX=40 EndY=11 EndZ=0
    g1: LineSegment StartX=40 StartY=11 StartZ=0 EndX=40 EndY=-7 EndZ=0
    g2: LineSegment StartX=40 StartY=-7 StartZ=0 EndX=-40 EndY=-7 EndZ=0
    g3: LineSegment StartX=-40 StartY=-7 StartZ=0 EndX=-40 EndY=11 EndZ=0
  constraints (11):
    c: Coincident(g0,g1)
    c: Coincident(g1,g2)
    c: Coincident(g2,g3)
    c: Coincident(g3,g0)
    c: Horizontal(g0)
    c: Vertical(g1)
    c: Vertical(g3)
    c: Symmetric(g1,g2,g-2)
    c: DistanceY(g0) = 11
    c: DistanceY(g1,g-1) = 7
    c: DistanceX(g0,g0) = 80
FEATURE [PartDesign::Pad] Pad
  AddSubType = 0
  AutoTaperInnerAngle = false
  CheckUpToFaceLimits = true
  ClaimChildren = false
  Direction = (1,1,1)
  Fit = 0
  FitJoin = 0
  InnerFit = 0
  InnerFitJoin = 0
  InvalidShape = false
  Length = 8
  Length2 = 100
  Linearize = true
  NewSolid = false
  Placement = pos=(0,0,0) rot=(1,0,0;1.5708rad)
  Profile = -> Sketch
  Refine = true
  Suppress = false
  TaperInnerAngle = 0
  TaperInnerAngleRev = 0
  TreeRank = 0
  Type = 0
  ValidateShape = true
  _ProfileBasedVersion = 1
FEATURE [Sketcher::SketchObject] Sketch001
  ArcFitTolerance = 0
  AttachmentSupport = -> [Pad]
  ExternalBSplineMaxDegree = 0
  ExternalBSplineTolerance = 0
  ExternalGeometry = -> [Pad]
  FullyConstrained = true
  InternalTolerance = 1e-06
  InvalidShape = false
  MakeInternals = false
  MapMode = 5
  Placement = pos=(40,0,0) rot=(0.707107,0,0.707107;3.14159rad)
  Support = -> [Pad]
  TreeRank = 0
  ValidateShape = true
  sketch-geometry (4):
    g0: Circle CenterX=-2.5 CenterY=4 CenterZ=0 NormalX=0 NormalY=0 NormalZ=1 AngleXU=0 Radius=2.05
    g1: Circle CenterX=6.5 CenterY=4 CenterZ=0 NormalX=0 NormalY=0 NormalZ=1 AngleXU=0 Radius=2.05
    g2: LineSegment [constr] StartX=-7 StartY=4 StartZ=0 EndX=11 EndY=4 EndZ=0
    g3: LineSegment [constr] StartX=2 StartY=8 StartZ=0 EndX=2 EndY=0 EndZ=0
  constraints (10):
    c: Horizontal(g1,g0)
    c: PointOnObject(g2,g-5)
    c: Horizontal(g2)
    c: PointOnObject(g3,g-1)
    c: Symmetric(g-4,g-4,g2)
    c: Symmetric(g-4,g-5,g3)
    c: Equal(g0,g1)
    c: Symmetric(g0,g1,g3)
    c: Diameter(g1) = 4.1
    c: Symmetric(g-5,g3,g0)
FEATURE [PartDesign::Pocket] Pocket
  AddSubType = 1
  AutoTaperInnerAngle = false
  BaseFeature = -> Pad
  CheckUpToFaceLimits = true
  ClaimChildren = false
  Fit = 0
  FitJoin = 0
  InnerFit = 0
  InnerFitJoin = 0
  InvalidShape = false
  Length = 12
  Length2 = 100
  Linearize = true
  NewSolid = false
  Placement = pos=(0,0,0) rot=(1,0,0;1.5708rad)
  Profile = -> Sketch001
  Refine = true
  Suppress = false
  TaperInnerAngle = 0
  TaperInnerAngleRev = 0
  TreeRank = 0
  Type = 0
  ValidateShape = true
  _ProfileBasedVersion = 1
  _Version = 1
FEATURE [PartDesign::Mirrored] Mirrored005
  AddSubType = 0
  BaseFeature = -> Pocket
  CopyShape = false
  InvalidShape = false
  MirrorPlane = -> YZ_Plane
  NewSolid = false
  OriginalSubs = -> [Pocket]
  Originals = -> [Pocket]
  ParallelTransform = true
  Placement = pos=(0,0,0) rot=(1,0,0;1.5708rad)
  Refine = true
  SubTransform = true
  Suppress = false
  TreeRank = 0
  ValidateShape = true
  _Version = 3
FEATURE [PartDesign::Chamfer] Chamfer
  AddSubType = 0
  Angle = 45
  Base = -> Mirrored005 [Edge9,Edge8,Edge13,Edge14]
  BaseFeature = -> Mirrored005
  ChamferType = 0
  FlipDirection = false
  InvalidShape = false
  NewSolid = false
  Placement = pos=(0,0,0) rot=(1,0,0;1.5708rad)
  Refine = true
  Size = 0.4
  Size2 = 1
  SupportTransform = false
  Suppress = false
  TreeRank = 0
  ValidateShape = true
FEATURE [PartDesign::Chamfer] Chamfer001
  AddSubType = 0
  Angle = 45
  Base = -> Chamfer [Edge11,Edge10,Edge12]
  BaseFeature = -> Chamfer
  ChamferType = 0
  FlipDirection = false
  InvalidShape = false
  NewSolid = false
  Placement = pos=(0,0,0) rot=(1,0,0;1.5708rad)
  Refine = true
  Size = 0.4
  Size2 = 1
  SupportTransform = false
  Suppress = false
  TreeRank = 0
  ValidateShape = true
FEATURE [PartDesign::Fillet] Fillet
  AddSubType = 0
  Base = -> Chamfer001 [Edge20]
  BaseFeature = -> Chamfer001
  InvalidShape = false
  NewSolid = false
  Placement = pos=(0,0,0) rot=(1,0,0;1.5708rad)
  Radius = 2
  Refine = true
  SupportTransform = false
  Suppress = false
  TreeRank = 0
  ValidateShape = true
FEATURE [PartDesign::Pocket] Pocket001
  AddSubType = 1
  AutoTaperInnerAngle = false
  BaseFeature = -> Fillet
  CheckUpToFaceLimits = true
  ClaimChildren = false
  Fit = 0
  FitJoin = 0
  InnerFit = 0
  InnerFitJoin = 0
  InvalidShape = false
  Length = 0.5
  Length2 = 100
  Linearize = true
  NewSolid = false
  Placement = pos=(0,0,0) rot=(1,0,0;1.5708rad)
  Profile = -> ShapeString
  Refine = true
  Suppress = false
  TaperInnerAngle = 0
  TaperInnerAngleRev = 0
  TreeRank = 0
  Type = 0
  ValidateShape = true
  _ProfileBasedVersion = 1
  _Version = 1
FEATURE [PartDesign::Body] Body  label="Front"
  AutoGroupSolids = false
  ClaimAllChildren = false
  ExportMode = 0
  Group = -> [Sketch,Pad,Sketch001,Pocket,Mirrored005,Chamfer,Chamfer001,Fillet,ShapeString,Pocket001]
  InvalidShape = false
  Origin = -> Origin
  Placement = pos=(-6.99382e-06,40,0) rot=(0,0,1;3.14159rad)
  SingleSolid = true
  Tip = -> Pocket001
  TreeRank = 0
  ValidateShape = true
  _ExportChildren = -> [Pad,Pocket,Mirrored005,Chamfer,Chamfer001,Fillet,Pocket001]
  _GroupVersion = 1
FEATURE [Sketcher::SketchObject] Sketch058
  ArcFitTolerance = 0
  AttachmentSupport = -> [YZ_Plane034]
  ExternalBSplineMaxDegree = 0
  ExternalBSplineTolerance = 0
  FullyConstrained = true
  InternalTolerance = 1e-06
  InvalidShape = false
  MakeInternals = false
  MapMode = 5
  Placement = pos=(0,0,0) rot=(0.57735,0.57735,0.57735;2.0944rad)
  Support = -> [YZ_Plane034]
  TreeRank = 0
  ValidateShape = true
  sketch-geometry (10):
    g0: LineSegment StartX=-8 StartY=-7 StartZ=0 EndX=-8 EndY=11 EndZ=0
    g1: LineSegment StartX=-8 StartY=11 StartZ=0 EndX=0 EndY=11 EndZ=0
    g2: LineSegment StartX=0 StartY=11 StartZ=0 EndX=47 EndY=7 EndZ=0
    g3: LineSegment StartX=47 StartY=7 StartZ=0 EndX=47 EndY=-7 EndZ=0
    g4: LineSegment StartX=47 StartY=-7 StartZ=0 EndX=-8 EndY=-7 EndZ=0
    g5: Circle CenterX=40 CenterY=0 CenterZ=0 NormalX=0 NormalY=0 NormalZ=1 AngleXU=0 Radius=4
    g6: Circle CenterX=-4 CenterY=6.5 CenterZ=0 NormalX=0 NormalY=0 NormalZ=1 AngleXU=0 Radius=1.6
    g7: Circle CenterX=-4 CenterY=-2.5 CenterZ=0 NormalX=0 NormalY=0 NormalZ=1 AngleXU=0 Radius=1.6
    g8: LineSegment [constr] StartX=-4 StartY=11 StartZ=0 EndX=-4 EndY=-7 EndZ=0
    g9: LineSegment [constr] StartX=-8 StartY=2 StartZ=0 EndX=0 EndY=2 EndZ=0
  constraints (27):
    c: Vertical(g0)
    c: Coincident(g0,g1)
    c: PointOnObject(g1,g-2)
    c: Horizontal(g1)
    c: Coincident(g1,g2)
    c: Coincident(g2,g3)
    c: Coincident(g3,g4)
    c: Coincident(g4,g0)
    c: Horizontal(g4)
    c: DistanceY(g0) = -7
    c: DistanceY(g0) = 11
    c: PointOnObject(g5,g-1)
    c: DistanceX(g5) = 40
    c: Symmetric(g2,g3,g-1)
    c: Diameter(g5) = 8
    c: DistanceX(g2) = 47
    c: DistanceX(g1,g1) = 8
    c: Vertical(g7,g6)
    c: PointOnObject(g8,g4)
    c: Vertical(g8)
    c: PointOnObject(g9,g-2)
    c: Symmetric(g0,g0,g9)
    c: Symmetric(g0,g1,g8)
    c: Symmetric(g6,g7,g9)
    c: Diameter(g6) = 3.2
    c: Equal(g6,g7)
    c: Symmetric(g9,g1,g6)
FEATURE [PartDesign::Pad] Pad032
  AddSubType = 0
  AutoTaperInnerAngle = false
  CheckUpToFaceLimits = true
  ClaimChildren = false
  Direction = (1,1,1)
  Fit = 0
  FitJoin = 0
  InnerFit = 0
  InnerFitJoin = 0
  InvalidShape = false
  Length = 3
  Length2 = 100
  Linearize = true
  NewSolid = false
  Placement = pos=(0,0,0) rot=(0.57735,0.57735,0.57735;2.0944rad)
  Profile = -> Sketch058
  Refine = true
  Suppress = false
  TaperInnerAngle = 0
  TaperInnerAngleRev = 0
  TreeRank = 0
  Type = 0
  ValidateShape = true
  _ProfileBasedVersion = 1
FEATURE [PartDesign::Fillet] Fillet017
  AddSubType = 0
  Base = -> Pad032 [Edge2]
  BaseFeature = -> Pad032
  InvalidShape = false
  NewSolid = false
  Placement = pos=(0,0,0) rot=(0.57735,0.57735,0.57735;2.0944rad)
  Radius = 2
  Refine = true
  SupportTransform = false
  Suppress = false
  TreeRank = 0
  ValidateShape = true
FEATURE [PartDesign::Fillet] Fillet020
  AddSubType = 0
  Base = -> Fillet017 [Edge24,Edge15]
  BaseFeature = -> Fillet017
  InvalidShape = false
  NewSolid = false
  Placement = pos=(0,0,0) rot=(0.57735,0.57735,0.57735;2.0944rad)
  Radius = 7.1
  Refine = true
  SupportTransform = false
  Suppress = false
  TreeRank = 0
  ValidateShape = true
FEATURE [PartDesign::Chamfer] Chamfer016
  AddSubType = 0
  Angle = 45
  Base = -> Fillet020 [Edge13]
  BaseFeature = -> Fillet020
  ChamferType = 0
  FlipDirection = false
  InvalidShape = false
  NewSolid = false
  Placement = pos=(0,0,0) rot=(0.57735,0.57735,0.57735;2.0944rad)
  Refine = true
  Size = 0.4
  Size2 = 1
  SupportTransform = false
  Suppress = false
  TreeRank = 0
  ValidateShape = true
FEATURE [PartDesign::Body] Body027  label="Lateral"
  AutoGroupSolids = false
  ClaimAllChildren = false
  ExportMode = 0
  Group = -> [Sketch058,Pad032,Fillet017,Fillet020,Chamfer016]
  InvalidShape = false
  Origin = -> Origin044
  Placement = pos=(-40,40,0) rot=(0,0,1;3.14159rad)
  SingleSolid = true
  Tip = -> Chamfer016
  TreeRank = 0
  ValidateShape = true
  _ExportChildren = -> [Pad032,Fillet017,Fillet020,Chamfer016]
  _GroupVersion = 1
FEATURE [Sketcher::SketchObject] Sketch059
  ArcFitTolerance = 0
  AttachmentSupport = -> [YZ_Plane035]
  ExternalBSplineMaxDegree = 0
  ExternalBSplineTolerance = 0
  FullyConstrained = true
  InternalTolerance = 1e-06
  InvalidShape = false
  MakeInternals = false
  MapMode = 5
  Placement = pos=(0,0,0) rot=(0.57735,0.57735,0.57735;2.0944rad)
  Support = -> [YZ_Plane035]
  TreeRank = 0
  ValidateShape = true
  sketch-geometry (10):
    g0: LineSegment StartX=-8 StartY=-7 StartZ=0 EndX=-8 EndY=11 EndZ=0
    g1: LineSegment StartX=-8 StartY=11 StartZ=0 EndX=0 EndY=11 EndZ=0
    g2: LineSegment StartX=0 StartY=11 StartZ=0 EndX=47 EndY=7 EndZ=0
    g3: LineSegment StartX=47 StartY=7 StartZ=0 EndX=47 EndY=-7 EndZ=0
    g4: LineSegment StartX=47 StartY=-7 StartZ=0 EndX=-8 EndY=-7 EndZ=0
    g5: Circle CenterX=40 CenterY=0 CenterZ=0 NormalX=0 NormalY=0 NormalZ=1 AngleXU=0 Radius=1.7
    g6: Circle CenterX=-4 CenterY=6.5 CenterZ=0 NormalX=0 NormalY=0 NormalZ=1 AngleXU=0 Radius=1.6
    g7: Circle CenterX=-4 CenterY=-2.5 CenterZ=0 NormalX=0 NormalY=0 NormalZ=1 AngleXU=0 Radius=1.6
    g8: LineSegment [constr] StartX=-4 StartY=11 StartZ=0 EndX=-4 EndY=-7 EndZ=0
    g9: LineSegment [constr] StartX=-8 StartY=2 StartZ=0 EndX=0 EndY=2 EndZ=0
  constraints (27):
    c: Vertical(g0)
    c: Coincident(g0,g1)
    c: PointOnObject(g1,g-2)
    c: Horizontal(g1)
    c: Coincident(g1,g2)
    c: Coincident(g2,g3)
    c: Coincident(g3,g4)
    c: Coincident(g4,g0)
    c: Horizontal(g4)
    c: DistanceY(g0) = -7
    c: DistanceY(g0) = 11
    c: PointOnObject(g5,g-1)
    c: DistanceX(g5) = 40
    c: Symmetric(g2,g3,g-1)
    c: Diameter(g5) = 3.4
    c: DistanceX(g2) = 47
    c: DistanceX(g1,g1) = 8
    c: Vertical(g7,g6)
    c: PointOnObject(g8,g4)
    c: Vertical(g8)
    c: PointOnObject(g9,g-2)
    c: Symmetric(g0,g0,g9)
    c: Symmetric(g0,g1,g8)
    c: Symmetric(g6,g7,g9)
    c: Diameter(g6) = 3.2
    c: Equal(g6,g7)
    c: Symmetric(g9,g1,g6)
FEATURE [PartDesign::Pad] Pad033
  AddSubType = 0
  AutoTaperInnerAngle = false
  CheckUpToFaceLimits = true
  ClaimChildren = false
  Direction = (1,1,1)
  Fit = 0
  FitJoin = 0
  InnerFit = 0
  InnerFitJoin = 0
  InvalidShape = false
  Length = 3
  Length2 = 100
  Linearize = true
  NewSolid = false
  Placement = pos=(0,0,0) rot=(0.57735,0.57735,0.57735;2.0944rad)
  Profile = -> Sketch059
  Refine = true
  Suppress = false
  TaperInnerAngle = 0
  TaperInnerAngleRev = 0
  TreeRank = 0
  Type = 0
  ValidateShape = true
  _ProfileBasedVersion = 1
FEATURE [PartDesign::Fillet] Fillet021
  AddSubType = 0
  Base = -> Pad033 [Edge2]
  BaseFeature = -> Pad033
  InvalidShape = false
  NewSolid = false
  Placement = pos=(0,0,0) rot=(0.57735,0.57735,0.57735;2.0944rad)
  Radius = 2
  Refine = true
  SupportTransform = false
  Suppress = false
  TreeRank = 0
  ValidateShape = true
FEATURE [PartDesign::Fillet] Fillet022
  AddSubType = 0
  Base = -> Fillet021 [Edge24,Edge15]
  BaseFeature = -> Fillet021
  InvalidShape = false
  NewSolid = false
  Placement = pos=(0,0,0) rot=(0.57735,0.57735,0.57735;2.0944rad)
  Radius = 7.1
  Refine = true
  SupportTransform = false
  Suppress = false
  TreeRank = 0
  ValidateShape = true
FEATURE [PartDesign::Chamfer] Chamfer017
  AddSubType = 0
  Angle = 45
  Base = -> Fillet022 [Edge13]
  BaseFeature = -> Fillet022
  ChamferType = 0
  FlipDirection = false
  InvalidShape = false
  NewSolid = false
  Placement = pos=(0,0,0) rot=(0.57735,0.57735,0.57735;2.0944rad)
  Refine = true
  Size = 0.4
  Size2 = 1
  SupportTransform = false
  Suppress = false
  TreeRank = 0
  ValidateShape = true
FEATURE [PartDesign::Body] Body028  label="Lateral001"
  AutoGroupSolids = false
  ClaimAllChildren = false
  ExportMode = 0
  Group = -> [Sketch059,Pad033,Fillet021,Fillet022,Chamfer017]
  InvalidShape = false
  Origin = -> Origin045
  Placement = pos=(-43,40,-8.9e-15) rot=(0,0,1;3.14159rad)
  SingleSolid = true
  Tip = -> Chamfer017
  TreeRank = 0
  ValidateShape = true
  _ExportChildren = -> [Pad033,Fillet021,Fillet022,Chamfer017]
  _GroupVersion = 1
COMPONENT P4 — recipe-attached ("SupportGauche3D", modeled in this document).
Construction recipe (the document's own serialized feature program — sketch geometry with constraints, then the solid features built on it; lengths are millimeters unless a unit is written):

FEATURE [Sketcher::SketchObject] Sketch037
  ArcFitTolerance = 0
  AttachmentSupport = -> [XZ_Plane030]
  ExternalBSplineMaxDegree = 0
  ExternalBSplineTolerance = 0
  FullyConstrained = true
  InternalTolerance = 1e-06
  InvalidShape = false
  MakeInternals = false
  MapMode = 5
  Placement = pos=(0,0,0) rot=(1,0,0;1.5708rad)
  Support = -> [XZ_Plane030]
  TreeRank = 0
  ValidateShape = true
  sketch-geometry (6):
    g0: LineSegment StartX=-5 StartY=0 StartZ=0 EndX=15 EndY=0 EndZ=0
    g1: LineSegment StartX=15 StartY=0 StartZ=0 EndX=15 EndY=-7 EndZ=0
    g2: LineSegment StartX=15 StartY=-7 StartZ=0 EndX=5 EndY=-7 EndZ=0
    g3: LineSegment StartX=5 StartY=-7 StartZ=0 EndX=5 EndY=-32 EndZ=0
    g4: LineSegment StartX=5 StartY=-32 StartZ=0 EndX=-5 EndY=-32 EndZ=0
    g5: LineSegment StartX=-5 StartY=-32 StartZ=0 EndX=-5 EndY=0 EndZ=0
  constraints (18):
    c: PointOnObject(g0,g-1)
    c: Horizontal(g0)
    c: Coincident(g0,g1)
    c: Vertical(g1)
    c: Coincident(g1,g2)
    c: Horizontal(g2)
    c: Coincident(g2,g3)
    c: Vertical(g3)
    c: Coincident(g3,g4)
    c: Horizontal(g4)
    c: Coincident(g4,g5)
    c: Coincident(g5,g0)
    c: Vertical(g5)
    c: DistanceY(g1,g1) = 7
    c: DistanceX(g-1,g2) = 5
    c: DistanceX(g2,g2) = 10
    c: DistanceY(g3,g3) = 25
    c: DistanceX(g0,g-1) = 5
FEATURE [PartDesign::Pad] Pad024
  AddSubType = 0
  AutoTaperInnerAngle = false
  CheckUpToFaceLimits = true
  ClaimChildren = false
  Direction = (1,1,1)
  Fit = 0
  FitJoin = 0
  InnerFit = 0
  InnerFitJoin = 0
  InvalidShape = false
  Length = 10
  Length2 = 100
  Linearize = true
  NewSolid = false
  Placement = pos=(0,0,0) rot=(1,0,0;1.5708rad)
  Profile = -> Sketch037
  Refine = true
  Reversed = true
  Suppress = false
  TaperInnerAngle = 0
  TaperInnerAngleRev = 0
  TreeRank = 0
  Type = 0
  ValidateShape = true
  _ProfileBasedVersion = 1
FEATURE [PartDesign::Pad] Pad025
  AddSubType = 0
  AutoTaperInnerAngle = false
  BaseFeature = -> Pad024
  CheckUpToFaceLimits = true
  ClaimChildren = false
  Direction = (1,1,1)
  Fit = 0
  FitJoin = 0
  InnerFit = 0
  InnerFitJoin = 0
  InvalidShape = false
  Length = 5
  Length2 = 100
  Linearize = true
  NewSolid = false
  Placement = pos=(0,0,0) rot=(1,0,0;1.5708rad)
  Profile = -> Sketch037
  Refine = true
  Suppress = false
  TaperInnerAngle = 0
  TaperInnerAngleRev = 0
  TreeRank = 0
  Type = 0
  ValidateShape = true
  _ProfileBasedVersion = 1
FEATURE [Sketcher::SketchObject] Sketch038
  ArcFitTolerance = 0
  AttachmentSupport = -> [XZ_Plane030]
  ExternalBSplineMaxDegree = 0
  ExternalBSplineTolerance = 0
  ExternalGeometry = -> [Pad025]
  FullyConstrained = true
  InternalTolerance = 1e-06
  InvalidShape = false
  MakeInternals = false
  MapMode = 5
  Placement = pos=(0,0,0) rot=(1,0,0;1.5708rad)
  Support = -> [XZ_Plane030]
  TreeRank = 0
  ValidateShape = true
  sketch-geometry (4):
    g0: LineSegment StartX=0 StartY=0 StartZ=0 EndX=-5 EndY=0 EndZ=0
    g1: LineSegment StartX=-5 StartY=0 StartZ=0 EndX=-5 EndY=-32 EndZ=0
    g2: LineSegment StartX=-5 StartY=-32 StartZ=0 EndX=0 EndY=-32 EndZ=0
    g3: LineSegment StartX=0 StartY=-32 StartZ=0 EndX=0 EndY=0 EndZ=0
  constraints (10):
    c: Coincident(g0,g1)
    c: Coincident(g1,g2)
    c: Coincident(g2,g3)
    c: Coincident(g3,g0)
    c: Horizontal(g0)
    c: Horizontal(g2)
    c: Vertical(g1)
    c: Vertical(g3)
    c: Coincident(g0,g-1)
    c: Coincident(g-3,g1)
FEATURE [PartDesign::Pocket] Pocket013
  AddSubType = 1
  AutoTaperInnerAngle = false
  BaseFeature = -> Pad025
  CheckUpToFaceLimits = true
  ClaimChildren = false
  Fit = 0
  FitJoin = 0
  InnerFit = 0
  InnerFitJoin = 0
  InvalidShape = false
  Length = 5
  Length2 = 100
  Linearize = true
  NewSolid = false
  Placement = pos=(0,0,0) rot=(1,0,0;1.5708rad)
  Profile = -> Sketch038
  Refine = true
  Suppress = false
  TaperInnerAngle = 0
  TaperInnerAngleRev = 0
  TreeRank = 0
  Type = 1
  ValidateShape = true
  _ProfileBasedVersion = 1
  _Version = 0
FEATURE [Sketcher::SketchObject] Sketch039
  ArcFitTolerance = 0
  AttachmentSupport = -> [Pocket013]
  ExternalBSplineMaxDegree = 0
  ExternalBSplineTolerance = 0
  ExternalGeometry = -> [Pocket013]
  FullyConstrained = true
  InternalTolerance = 1e-06
  InvalidShape = false
  MakeInternals = false
  MapMode = 5
  Placement = pos=(0,-5,-1.1e-15) rot=(1,0,0;1.5708rad)
  Support = -> [Pocket013]
  TreeRank = 0
  ValidateShape = true
  sketch-geometry (3):
    g0: LineSegment StartX=15 StartY=-7 StartZ=0 EndX=5 EndY=-19.5 EndZ=0
    g1: LineSegment StartX=5 StartY=-7 StartZ=0 EndX=5 EndY=-19.5 EndZ=0
    g2: LineSegment StartX=5 StartY=-7 StartZ=0 EndX=15 EndY=-7 EndZ=0
  constraints (6):
    c: Coincident(g0,g-3)
    c: Coincident(g1,g-4)
    c: Coincident(g1,g0)
    c: Coincident(g2,g1)
    c: Coincident(g2,g0)
    c: Symmetric(g1,g-4,g0)
FEATURE [PartDesign::Pad] Pad026
  AddSubType = 0
  AutoTaperInnerAngle = false
  BaseFeature = -> Pocket013
  CheckUpToFaceLimits = true
  ClaimChildren = false
  Direction = (1,1,1)
  Fit = 0
  FitJoin = 0
  InnerFit = 0
  InnerFitJoin = 0
  InvalidShape = false
  Length = 2
  Length2 = 100
  Linearize = true
  NewSolid = false
  Placement = pos=(0,0,0) rot=(1,0,0;1.5708rad)
  Profile = -> Sketch039
  Refine = true
  Reversed = true
  Suppress = false
  TaperInnerAngle = 0
  TaperInnerAngleRev = 0
  TreeRank = 0
  Type = 0
  ValidateShape = true
  _ProfileBasedVersion = 1
FEATURE [Sketcher::SketchObject] Sketch040
  ArcFitTolerance = 0
  AttachmentSupport = -> [XY_Plane030]
  ExternalBSplineMaxDegree = 0
  ExternalBSplineTolerance = 0
  ExternalGeometry = -> [Pad026]
  FullyConstrained = true
  InternalTolerance = 1e-06
  InvalidShape = false
  MakeInternals = false
  MapMode = 5
  Support = -> [XY_Plane030]
  TreeRank = 0
  ValidateShape = true
  sketch-geometry (1):
    g0: Circle CenterX=10 CenterY=5 CenterZ=0 NormalX=0 NormalY=0 NormalZ=1 AngleXU=0 Radius=2.05
  constraints (3):
    c: DistanceX(g0,g-3) = 5
    c: DistanceY(g0,g-3) = 5
    c: Diameter(g0) = 4.1
FEATURE [PartDesign::Pocket] Pocket014
  AddSubType = 1
  AutoTaperInnerAngle = false
  BaseFeature = -> Pad026
  CheckUpToFaceLimits = true
  ClaimChildren = false
  Fit = 0
  FitJoin = 0
  InnerFit = 0
  InnerFitJoin = 0
  InvalidShape = false
  Length = 5
  Length2 = 100
  Linearize = true
  NewSolid = false
  Placement = pos=(0,0,0) rot=(1,0,0;1.5708rad)
  Profile = -> Sketch040
  Refine = true
  Suppress = false
  TaperInnerAngle = 0
  TaperInnerAngleRev = 0
  TreeRank = 0
  Type = 1
  ValidateShape = true
  _ProfileBasedVersion = 1
  _Version = 0
FEATURE [Sketcher::SketchObject] Sketch041
  ArcFitTolerance = 0
  AttachmentSupport = -> [Pocket014]
  ExternalBSplineMaxDegree = 0
  ExternalBSplineTolerance = 0
  ExternalGeometry = -> [Pocket014]
  FullyConstrained = true
  InternalTolerance = 1e-06
  InvalidShape = false
  MakeInternals = false
  MapMode = 5
  Placement = pos=(5,0,0) rot=(0.707107,0,0.707107;3.14159rad)
  Support = -> [Pocket014]
  TreeRank = 0
  ValidateShape = true
  sketch-geometry (4):
    g0: Circle CenterX=-27 CenterY=-5 CenterZ=0 NormalX=0 NormalY=0 NormalZ=1 AngleXU=0 Radius=1.6
    g1: Circle CenterX=-12 CenterY=-5 CenterZ=0 NormalX=0 NormalY=0 NormalZ=1 AngleXU=0 Radius=1.6
    g2: LineSegment [constr] StartX=-32 StartY=-5 StartZ=0 EndX=-7 EndY=-5 EndZ=0
    g3: GeomPoint [constr] X=-19.5 Y=-5 Z=0
  constraints (10):
    c: Diameter(g0) = 3.2
    c: Equal(g0,g1)
    c: Horizontal(g1,g0)
    c: PointOnObject(g2,g-4)
    c: PointOnObject(g2,g-3)
    c: Horizontal(g2)
    c: DistanceY(g-5,g2) = 5
    c: Symmetric(g2,g2,g3)
    c: Symmetric(g0,g1,g3)
    c: DistanceX(g2,g0) = 5
FEATURE [PartDesign::Pocket] Pocket015
  AddSubType = 1
  AutoTaperInnerAngle = false
  BaseFeature = -> Pocket014
  CheckUpToFaceLimits = true
  ClaimChildren = false
  Fit = 0
  FitJoin = 0
  InnerFit = 0
  InnerFitJoin = 0
  InvalidShape = false
  Length = 5
  Length2 = 100
  Linearize = true
  NewSolid = false
  Placement = pos=(0,0,0) rot=(1,0,0;1.5708rad)
  Profile = -> Sketch041
  Refine = true
  Suppress = false
  TaperInnerAngle = 0
  TaperInnerAngleRev = 0
  TreeRank = 0
  Type = 1
  ValidateShape = true
  _ProfileBasedVersion = 1
  _Version = 0
FEATURE [Sketcher::SketchObject] Sketch042
  ArcFitTolerance = 0
  AttachmentSupport = -> [Pocket015]
  ExternalBSplineMaxDegree = 0
  ExternalBSplineTolerance = 0
  ExternalGeometry = -> [Pocket015]
  FullyConstrained = true
  InternalTolerance = 1e-06
  InvalidShape = false
  MakeInternals = false
  MapMode = 5
  Placement = pos=(5,0,0) rot=(0.707107,0,0.707107;3.14159rad)
  Support = -> [Pocket015]
  TreeRank = 0
  ValidateShape = true
  sketch-geometry (5):
    g0: LineSegment StartX=-32 StartY=-10 StartZ=0 EndX=-32 EndY=-0.75 EndZ=0
    g1: LineSegment StartX=-32 StartY=-10 StartZ=0 EndX=-7.75 EndY=-10 EndZ=0
    g2: LineSegment StartX=-7.75 StartY=-10 StartZ=0 EndX=-7.75 EndY=-5 EndZ=0
    g3: ArcOfCircle CenterX=-12 CenterY=-5 CenterZ=0 NormalX=0 NormalY=0 NormalZ=1 AngleXU=0 Radius=4.25 StartAngle=0 EndAngle=1.5708
    g4: LineSegment StartX=-32 StartY=-0.75 StartZ=0 EndX=-12 EndY=-0.75 EndZ=0
  constraints (12):
    c: Coincident(g0,g-4)
    c: PointOnObject(g0,g-3)
    c: Coincident(g1,g0)
    c: PointOnObject(g1,g-4)
    c: Coincident(g2,g1)
    c: Vertical(g2)
    c: Coincident(g4,g0)
    c: Horizontal(g4)
    c: Tangent(g4,g3) = 1.5708
    c: Tangent(g3,g2) = -1.5708
    c: Coincident(g3,g-5)
    c: Diameter(g3) = 8.5
FEATURE [PartDesign::Pocket] Pocket016
  AddSubType = 1
  AutoTaperInnerAngle = false
  BaseFeature = -> Pocket015
  CheckUpToFaceLimits = true
  ClaimChildren = false
  Fit = 0
  FitJoin = 0
  InnerFit = 0
  InnerFitJoin = 0
  InvalidShape = false
  Length = 2.5
  Length2 = 100
  Linearize = true
  NewSolid = false
  Placement = pos=(0,0,0) rot=(1,0,0;1.5708rad)
  Profile = -> Sketch042
  Refine = true
  Suppress = false
  TaperInnerAngle = 0
  TaperInnerAngleRev = 0
  TreeRank = 0
  Type = 0
  ValidateShape = true
  _ProfileBasedVersion = 1
  _Version = 0
FEATURE [PartDesign::Chamfer] Chamfer006
  AddSubType = 0
  Angle = 45
  Base = -> Pocket016 [Edge46,Edge41,Edge42,Edge39,Edge40,Edge36]
  BaseFeature = -> Pocket016
  ChamferType = 0
  FlipDirection = false
  InvalidShape = false
  NewSolid = false
  Placement = pos=(0,0,0) rot=(1,0,0;1.5708rad)
  Refine = true
  Size = 0.2
  Size2 = 1
  SupportTransform = false
  Suppress = false
  TreeRank = 0
  ValidateShape = true
FEATURE [PartDesign::Chamfer] Chamfer005
  AddSubType = 0
  Angle = 45
  Base = -> Chamfer006 [Edge9,Edge36,Edge45,Edge21,Edge13]
  BaseFeature = -> Chamfer006
  ChamferType = 0
  FlipDirection = false
  InvalidShape = false
  NewSolid = false
  Placement = pos=(0,0,0) rot=(1,0,0;1.5708rad)
  Refine = true
  Size = 1
  Size2 = 1
  SupportTransform = false
  Suppress = false
  TreeRank = 0
  ValidateShape = true
FEATURE [PartDesign::Body] Body023  label="BodySupport3DInter"
  AutoGroupSolids = false
  ClaimAllChildren = false
  ExportMode = 0
  Group = -> [Sketch037,Pad024,Pad025,Sketch038,Pocket013,Sketch039,Pad026,Sketch040,Pocket014,Sketch041,Pocket015,Sketch042,Pocket016,Chamfer006,Chamfer005]
  InvalidShape = false
  Origin = -> Origin034
  SingleSolid = true
  Tip = -> Chamfer005
  TreeRank = 0
  ValidateShape = true
  _ExportChildren = -> [Pad024,Pad025,Pocket013,Pad026,Pocket014,Pocket015,Pocket016,Chamfer006,Chamfer005]
  _GroupVersion = 1
COMPONENT P5 — geometry summary ("SupportDroit3D"; no construction recipe available for this part):
  bounding box: 32.0 x 20.0 x 15.0 mm
  tessellated surface: 3,310 triangles
  volume: 3677 mm^3 (38% of its bounding box)
COMPONENT P6 — recipe-attached ("PartSideModule", modeled in this document).
Construction recipe (the document's own serialized feature program — sketch geometry with constraints, then the solid features built on it; lengths are millimeters unless a unit is written):

FEATURE [Sketcher::SketchObject] Sketch045
  ArcFitTolerance = 0
  AttachmentSupport = -> [XY_Plane032]
  ExternalBSplineMaxDegree = 0
  ExternalBSplineTolerance = 0
  FullyConstrained = true
  InternalTolerance = 1e-06
  InvalidShape = false
  MakeInternals = false
  MapMode = 5
  Support = -> [XY_Plane032]
  TreeRank = 0
  ValidateShape = true
  sketch-geometry (6):
    g0: LineSegment StartX=40 StartY=50 StartZ=0 EndX=40 EndY=40 EndZ=0
    g1: LineSegment StartX=40 StartY=40 StartZ=0 EndX=47.3205 EndY=27.3205 EndZ=0
    g2: LineSegment [constr] StartX=0 StartY=0 StartZ=0 EndX=54.6506 EndY=31.5526 EndZ=0
    g3: LineSegment StartX=40 StartY=50 StartZ=0 EndX=44 EndY=50 EndZ=0
    g4: LineSegment StartX=44 StartY=50 StartZ=0 EndX=54.6506 EndY=31.5526 EndZ=0
    g5: LineSegment StartX=54.6506 StartY=31.5526 StartZ=0 EndX=47.3205 EndY=27.3205 EndZ=0
  constraints (17):
    c: Vertical(g0)
    c: Coincident(g1,g0)
    c: Coincident(g2,g-1)
    c: Angle(g2,g-2) = 1.0472
    c: PointOnObject(g1,g2)
    c: Coincident(g0,g3)
    c: Horizontal(g3)
    c: Coincident(g3,g4)
    c: Coincident(g4,g5)
    c: Coincident(g5,g1)
    c: Parallel(g1,g4)
    c: DistanceX(g2,g0) = 40
    c: DistanceY(g0,g0) = 10
    c: DistanceY(g0) = 40
    c: Perpendicular(g5,g1)
    c: DistanceX(g3,g3) = 4
    c: Coincident(g2,g4)
FEATURE [PartDesign::Plane] DatumPlane004
  AttachmentOffset = pos=(0,0,0) rot=(0,-1,0;1.0472rad)
  AttachmentSupport = -> [YZ_Plane032]
  InvalidShape = false
  Length = 81.5526
  MapMode = 5
  MinimumLength = 10
  MinimumWidth = 10
  Placement = pos=(0,0,0) rot=(0.935113,0.250563,0.250563;1.63783rad)
  ResizeMode = 0
  Support = -> [YZ_Plane032]
  TreeRank = 0
  ValidateShape = true
  Width = 30
FEATURE [PartDesign::Pad] Pad028
  AddSubType = 0
  AutoTaperInnerAngle = false
  CheckUpToFaceLimits = true
  ClaimChildren = false
  Direction = (1,1,1)
  Fit = 0
  FitJoin = 0
  InnerFit = 0
  InnerFitJoin = 0
  InvalidShape = false
  Length = 30
  Length2 = 100
  Linearize = true
  Midplane = true
  NewSolid = false
  Profile = -> Sketch045
  Refine = true
  Suppress = false
  TaperInnerAngle = 0
  TaperInnerAngleRev = 0
  TreeRank = 0
  Type = 0
  ValidateShape = true
  _ProfileBasedVersion = 1
FEATURE [PartDesign::Mirrored] Mirrored
  AddSubType = 0
  BaseFeature = -> Pad028
  CopyShape = false
  InvalidShape = false
  MirrorPlane = -> DatumPlane004
  NewSolid = false
  OriginalSubs = -> [Pad028]
  Originals = -> [Pad028]
  ParallelTransform = true
  Refine = true
  SubTransform = true
  Suppress = false
  TreeRank = 0
  ValidateShape = true
  _Version = 2
FEATURE [Sketcher::SketchObject] Sketch046
  ArcFitTolerance = 0
  AttachmentOffset = pos=(0,0,-10) rot=(0,0,1;0rad)
  AttachmentSupport = -> [Mirrored]
  ExternalBSplineMaxDegree = 0
  ExternalBSplineTolerance = 0
  ExternalGeometry = -> [Mirrored]
  FullyConstrained = true
  InternalTolerance = 1e-06
  InvalidShape = false
  MakeInternals = false
  MapMode = 5
  Placement = pos=(50,0,0) rot=(0.57735,-0.57735,-0.57735;2.0944rad)
  Support = -> [Mirrored]
  TreeRank = 0
  ValidateShape = true
  sketch-geometry (2):
    g0: Circle CenterX=-45 CenterY=10 CenterZ=0 NormalX=0 NormalY=0 NormalZ=1 AngleXU=0 Radius=1.5
    g1: LineSegment [constr] StartX=-45 StartY=15 StartZ=0 EndX=-45 EndY=-15 EndZ=0
  constraints (6):
    c: Diameter(g0) = 3
    c: DistanceY(g0) = 10
    c: PointOnObject(g1,g-4)
    c: Vertical(g1)
    c: Symmetric(g-3,g-3,g1)
    c: PointOnObject(g0,g1)
FEATURE [PartDesign::Hole] Hole
  AddSubType = 1
  BaseFeature = -> Mirrored
  ClaimChildren = false
  CustomThreadClearance = 0
  Depth = 25
  DepthType = 0
  Diameter = 3.2
  DrillForDepth = false
  DrillPoint = 1
  DrillPointAngle = 118
  Fit = 0
  FitJoin = 0
  HoleCutCountersinkAngle = 90
  HoleCutCustomValues = false
  HoleCutDepth = 7.5
  HoleCutDiameter = 8.5
  HoleCutType = 1
  InnerFit = 0
  InnerFitJoin = 0
  InvalidShape = false
  ModelThread = false
  NewSolid = false
  Profile = -> Sketch046
  Refine = true
  Reversed = true
  Suppress = false
  Tapered = false
  TaperedAngle = 90
  ThreadClass = 0
  ThreadDepth = 23.5
  ThreadDepthType = 0
  ThreadDirection = 0
  ThreadFit = 0
  ThreadSize = 0
  ThreadType = 0
  Threaded = false
  TreeRank = 0
  UseCustomThreadClearance = false
  ValidateShape = true
  _ProfileBasedVersion = 1
FEATURE [PartDesign::Mirrored] Mirrored001
  AddSubType = 0
  CopyShape = false
  InvalidShape = false
  MirrorPlane = -> XY_Plane032
  NewSolid = false
  ParallelTransform = true
  Refine = true
  SubTransform = true
  Suppress = false
  TreeRank = 0
  ValidateShape = true
  _Version = 2
FEATURE [PartDesign::Mirrored] Mirrored002
  AddSubType = 0
  CopyShape = false
  InvalidShape = false
  MirrorPlane = -> DatumPlane004
  NewSolid = false
  ParallelTransform = true
  Refine = true
  SubTransform = true
  Suppress = false
  TreeRank = 0
  ValidateShape = true
  _Version = 2
FEATURE [PartDesign::MultiTransform] MultiTransform002
  AddSubType = 0
  BaseFeature = -> Hole
  CopyShape = false
  InvalidShape = false
  NewSolid = false
  OriginalSubs = -> [Hole]
  Originals = -> [Hole]
  ParallelTransform = true
  Refine = true
  SubTransform = true
  Suppress = false
  Transformations = -> [Mirrored001,Mirrored002]
  TreeRank = 0
  ValidateShape = true
  _Version = 2
FEATURE [Sketcher::SketchObject] Sketch047
  ArcFitTolerance = 0
  AttachmentSupport = -> [MultiTransform002]
  ExternalBSplineMaxDegree = 0
  ExternalBSplineTolerance = 0
  FullyConstrained = true
  InternalTolerance = 1e-06
  InvalidShape = false
  MakeInternals = false
  MapMode = 5
  Placement = pos=(54.6506,31.5526,-6.3e-15) rot=(0.377964,0.654654,0.654654;2.41886rad)
  Support = -> [MultiTransform002]
  TreeRank = 0
  ValidateShape = true
  sketch-geometry (1):
    g0: Circle CenterX=7.5 CenterY=10 CenterZ=0 NormalX=0 NormalY=0 NormalZ=1 AngleXU=0 Radius=2.05
  constraints (3):
    c: Diameter(g0) = 4.1
    c: DistanceY(g-1,g0) = 10
    c: DistanceX(g-1,g0) = 7.5
FEATURE [PartDesign::Pocket] Pocket018
  AddSubType = 1
  AutoTaperInnerAngle = false
  BaseFeature = -> MultiTransform002
  CheckUpToFaceLimits = true
  ClaimChildren = false
  Fit = 0
  FitJoin = 0
  InnerFit = 0
  InnerFitJoin = 0
  InvalidShape = false
  Length = 5
  Length2 = 100
  Linearize = true
  NewSolid = false
  Profile = -> Sketch047
  Refine = true
  Suppress = false
  TaperInnerAngle = 0
  TaperInnerAngleRev = 0
  TreeRank = 0
  Type = 1
  ValidateShape = true
  _ProfileBasedVersion = 1
  _Version = 0
FEATURE [PartDesign::Mirrored] Mirrored003
  AddSubType = 0
  CopyShape = false
  InvalidShape = false
  MirrorPlane = -> DatumPlane004
  NewSolid = false
  ParallelTransform = true
  Refine = true
  SubTransform = true
  Suppress = false
  TreeRank = 0
  ValidateShape = true
  _Version = 2
FEATURE [PartDesign::Mirrored] Mirrored004
  AddSubType = 0
  CopyShape = false
  InvalidShape = false
  MirrorPlane = -> XY_Plane032
  NewSolid = false
  ParallelTransform = true
  Refine = true
  SubTransform = true
  Suppress = false
  TreeRank = 0
  ValidateShape = true
  _Version = 2
FEATURE [PartDesign::MultiTransform] MultiTransform003
  AddSubType = 0
  BaseFeature = -> Pocket018
  CopyShape = false
  InvalidShape = false
  NewSolid = false
  OriginalSubs = -> [Pocket018]
  Originals = -> [Pocket018]
  ParallelTransform = true
  Refine = true
  SubTransform = true
  Suppress = false
  Transformations = -> [Mirrored003,Mirrored004]
  TreeRank = 0
  ValidateShape = true
  _Version = 2
FEATURE [PartDesign::Chamfer] Chamfer008
  AddSubType = 0
  Angle = 45
  Base = -> MultiTransform003 [Edge5,Edge6,Edge38,Edge37,Edge21,Edge19,Edge20,Edge22,Edge30,Edge29,Edge33,Edge34,Edge32,Edge28,Edge35,Edge31]
  BaseFeature = -> MultiTransform003
  ChamferType = 0
  FlipDirection = false
  InvalidShape = false
  NewSolid = false
  Refine = true
  Size = 0.2
  Size2 = 1
  SupportTransform = false
  Suppress = false
  TreeRank = 0
  ValidateShape = true
FEATURE [Sketcher::SketchObject] Sketch048
  ArcFitTolerance = 0
  AttachmentSupport = -> [Chamfer008]
  ExternalBSplineMaxDegree = 0
  ExternalBSplineTolerance = 0
  FullyConstrained = true
  InternalTolerance = 1e-06
  InvalidShape = false
  MakeInternals = false
  MapMode = 5
  Placement = pos=(54.6506,31.5526,-6.3e-15) rot=(0.377964,0.654654,0.654654;2.41886rad)
  Support = -> [Chamfer008]
  TreeRank = 0
  ValidateShape = true
  sketch-geometry (16):
    g0: ArcOfCircle CenterX=-15 CenterY=0 CenterZ=0 NormalX=0 NormalY=0 NormalZ=1 AngleXU=0 Radius=1 StartAngle=1.5708 EndAngle=4.71239
    g1: ArcOfCircle CenterX=15 CenterY=0 CenterZ=0 NormalX=0 NormalY=0 NormalZ=1 AngleXU=0 Radius=1 StartAngle=4.71239 EndAngle=7.85398
    g2: LineSegment [constr] StartX=-15 StartY=-1 StartZ=0 EndX=15 EndY=-1 EndZ=0
    g3: LineSegment [constr] StartX=-15 StartY=1 StartZ=0 EndX=15 EndY=1 EndZ=0
    g4: ArcOfCircle CenterX=2.81924e-11 CenterY=-10 CenterZ=0 NormalX=0 NormalY=0 NormalZ=1 AngleXU=0 Radius=1 StartAngle=3.14159 EndAngle=6.28319
    g5: ArcOfCircle CenterX=-2.81924e-11 CenterY=10 CenterZ=0 NormalX=0 NormalY=0 NormalZ=1 AngleXU=0 Radius=1 StartAngle=0 EndAngle=3.14159
    g6: LineSegment [constr] StartX=1 StartY=-10 StartZ=0 EndX=1 EndY=10 EndZ=0
    g7: LineSegment [constr] StartX=-1 StartY=-10 StartZ=0 EndX=-1 EndY=10 EndZ=0
    g8: LineSegment StartX=-15 StartY=1 StartZ=0 EndX=-1 EndY=1 EndZ=0
    g9: LineSegment StartX=-1 StartY=1 StartZ=0 EndX=-1 EndY=10 EndZ=0
    g10: LineSegment StartX=1 StartY=10 StartZ=0 EndX=1 EndY=1 EndZ=0
    g11: LineSegment StartX=1 StartY=1 StartZ=0 EndX=15 EndY=1 EndZ=0
    g12: LineSegment StartX=-15 StartY=-1 StartZ=0 EndX=-1 EndY=-1 EndZ=0
    g13: LineSegment StartX=-1 StartY=-1 StartZ=0 EndX=-1 EndY=-10 EndZ=0
    g14: LineSegment StartX=1 StartY=-10 StartZ=0 EndX=1 EndY=-1 EndZ=0
    g15: LineSegment StartX=1 StartY=-1 StartZ=0 EndX=15 EndY=-1 EndZ=0
  constraints (36):
    c: Tangent(g0,g3) = 1.5708
    c: Tangent(g0,g2) = -1.5708
    c: Tangent(g2,g1) = -1.5708
    c: Tangent(g3,g1) = 1.5708
    c: Horizontal(g2)
    c: Equal(g0,g1)
    c: Tangent(g4,g7) = 1.5708
    c: Tangent(g4,g6) = -1.5708
    c: Tangent(g6,g5) = -1.5708
    c: Tangent(g7,g5) = 1.5708
    c: Vertical(g6)
    c: Equal(g4,g5)
    c: Equal(g5,g0)
    c: Symmetric(g0,g1,g-1)
    c: Symmetric(g4,g5,g-1)
    c: Diameter(g0) = 2
    c: DistanceX(g0,g1) = 30
    c: DistanceY(g4,g5) = 20
    c: Tangent(g0,g8) = 1.5708
    c: Coincident(g8,g9)
    c: Coincident(g9,g5)
    c: Vertical(g9)
    c: Tangent(g5,g10) = 1.5708
    c: Coincident(g11,g10)
    c: Coincident(g11,g1)
    c: Horizontal(g11)
    c: Coincident(g12,g0)
    c: PointOnObject(g12,g7)
    c: Horizontal(g12)
    c: Coincident(g13,g12)
    c: Coincident(g13,g4)
    c: Coincident(g14,g4)
    c: PointOnObject(g14,g2)
    c: Vertical(g14)
    c: Coincident(g15,g14)
    c: Coincident(g15,g1)
FEATURE [PartDesign::Pocket] Pocket019
  AddSubType = 1
  AutoTaperInnerAngle = false
  BaseFeature = -> Chamfer008
  CheckUpToFaceLimits = true
  ClaimChildren = false
  Fit = 0
  FitJoin = 0
  InnerFit = 0
  InnerFitJoin = 0
  InvalidShape = false
  Length = 0.7
  Length2 = 100
  Linearize = true
  NewSolid = false
  Profile = -> Sketch048
  Refine = true
  Suppress = false
  TaperInnerAngle = 0
  TaperInnerAngleRev = 0
  TreeRank = 0
  Type = 0
  ValidateShape = true
  _ProfileBasedVersion = 1
  _Version = 0
FEATURE [PartDesign::Fillet] Fillet015
  AddSubType = 0
  Base = -> Pocket019 [Edge97,Edge79,Edge85,Edge91]
  BaseFeature = -> Pocket019
  InvalidShape = false
  NewSolid = false
  Radius = 0.5
  Refine = true
  SupportTransform = false
  Suppress = false
  TreeRank = 0
  ValidateShape = true
FEATURE [PartDesign::Body] Body025  label="BodyPartSide"
  AutoGroupSolids = false
  ClaimAllChildren = false
  ExportMode = 0
  Group = -> [Sketch045,DatumPlane004,Pad028,Mirrored,Sketch046,Hole,MultiTransform002,Mirrored001,Mirrored002,Sketch047,Pocket018,MultiTransform003,Chamfer008,Mirrored003,Mirrored004,Sketch048,Pocket019,Fillet015]
  InvalidShape = false
  Origin = -> Origin038
  SingleSolid = true
  Tip = -> Fillet015
  TreeRank = 0
  ValidateShape = true
  _ExportChildren = -> [DatumPlane004,Pad028,Mirrored,Hole,MultiTransform002,Pocket018,MultiTransform003,Chamfer008,Pocket019,Fillet015]
  _GroupVersion = 1
COMPONENT P7 — recipe-attached ("EnsembleSemelle", modeled in this document).
Construction recipe (the document's own serialized feature program — sketch geometry with constraints, then the solid features built on it; lengths are millimeters unless a unit is written):

FEATURE [Sketcher::SketchObject] Sketch032
  ArcFitTolerance = 0
  AttachmentSupport = -> [XY_Plane026]
  ExternalBSplineMaxDegree = 0
  ExternalBSplineTolerance = 0
  FullyConstrained = true
  InternalTolerance = 1e-06
  InvalidShape = false
  MakeInternals = false
  MapMode = 5
  Support = -> [XY_Plane026]
  TreeRank = 0
  ValidateShape = true
  sketch-geometry (56):
    g0: LineSegment StartX=-131.619 StartY=-24.0289 StartZ=0 EndX=-58.007 EndY=18.4711 EndZ=0
    g1: LineSegment StartX=-58.007 StartY=18.4711 StartZ=0 EndX=-45 EndY=41 EndZ=0
    g2: LineSegment StartX=-45 StartY=41 StartZ=0 EndX=-45 EndY=126 EndZ=0
    g3: LineSegment StartX=-45 StartY=126 StartZ=0 EndX=45 EndY=126 EndZ=0
    g4: LineSegment StartX=45 StartY=126 StartZ=0 EndX=45 EndY=41 EndZ=0
    g5: LineSegment StartX=45 StartY=41 StartZ=0 EndX=58.007 EndY=18.4711 EndZ=0
    g6: LineSegment StartX=58.007 StartY=18.4711 StartZ=0 EndX=131.619 EndY=-24.0289 EndZ=0
    g7: LineSegment StartX=131.619 StartY=-24.0289 StartZ=0 EndX=86.6192 EndY=-101.971 EndZ=0
    g8: LineSegment StartX=86.6192 StartY=-101.971 StartZ=0 EndX=13.007 EndY=-59.4711 EndZ=0
    g9: LineSegment StartX=13.007 StartY=-59.4711 StartZ=0 EndX=-13.007 EndY=-59.4711 EndZ=0
    g10: LineSegment StartX=-13.007 StartY=-59.4711 StartZ=0 EndX=-86.6192 EndY=-101.971 EndZ=0
    g11: LineSegment StartX=-86.6192 StartY=-101.971 StartZ=0 EndX=-131.619 EndY=-24.0289 EndZ=0
    g12: LineSegment [constr] StartX=-1e-16 StartY=1e-16 StartZ=0 EndX=-1e-16 EndY=126 EndZ=0
    g13: LineSegment [constr] StartX=-1e-16 StartY=1e-16 StartZ=0 EndX=-109.119 EndY=-63 EndZ=0
    g14: LineSegment [constr] StartX=-1e-16 StartY=1e-16 StartZ=0 EndX=109.119 EndY=-63 EndZ=0
    g15: LineSegment StartX=-27.5 StartY=40 StartZ=0 EndX=27.5 EndY=40 EndZ=0
    g16: LineSegment StartX=27.5 StartY=40 StartZ=0 EndX=27.5 EndY=105 EndZ=0
    g17: LineSegment StartX=27.5 StartY=105 StartZ=0 EndX=-27.5 EndY=105 EndZ=0
    g18: LineSegment StartX=-27.5 StartY=105 StartZ=0 EndX=-27.5 EndY=40 EndZ=0
    g19: LineSegment StartX=20.891 StartY=-43.8157 StartZ=0 EndX=48.391 EndY=3.8157 EndZ=0
    g20: LineSegment StartX=48.391 StartY=3.8157 StartZ=0 EndX=104.683 EndY=-28.6843 EndZ=0
    g21: LineSegment StartX=104.683 StartY=-28.6843 StartZ=0 EndX=77.1827 EndY=-76.3157 EndZ=0
    g22: LineSegment StartX=77.1827 StartY=-76.3157 StartZ=0 EndX=20.891 EndY=-43.8157 EndZ=0
    g23: LineSegment StartX=-104.683 StartY=-28.6843 StartZ=0 EndX=-77.1827 EndY=-76.3157 EndZ=0
    g24: LineSegment StartX=-77.1827 StartY=-76.3157 StartZ=0 EndX=-20.891 EndY=-43.8157 EndZ=0
    g25: LineSegment StartX=-20.891 StartY=-43.8157 StartZ=0 EndX=-48.391 EndY=3.8157 EndZ=0
    g26: LineSegment StartX=-48.391 StartY=3.8157 StartZ=0 EndX=-104.683 EndY=-28.6843 EndZ=0
    g27: Circle [constr] CenterX=-1e-16 CenterY=1e-16 CenterZ=0 NormalX=0 NormalY=0 NormalZ=1 AngleXU=0 Radius=48.5412
    g28: LineSegment StartX=-11.547 StartY=-20 StartZ=0 EndX=-23.094 EndY=0 EndZ=0
    g29: LineSegment StartX=-23.094 StartY=-1.3e-15 StartZ=0 EndX=-11.547 EndY=20 EndZ=0
    g30: LineSegment StartX=-11.547 StartY=20 StartZ=0 EndX=11.547 EndY=20 EndZ=0
    g31: LineSegment StartX=11.547 StartY=20 StartZ=0 EndX=23.094 EndY=0 EndZ=0
    g32: LineSegment StartX=23.094 StartY=9e-16 StartZ=0 EndX=11.547 EndY=-20 EndZ=0
    g33: LineSegment StartX=11.547 StartY=-20 StartZ=0 EndX=-11.547 EndY=-20 EndZ=0
    g34: Circle [constr] CenterX=-1e-16 CenterY=1e-16 CenterZ=0 NormalX=0 NormalY=0 NormalZ=1 AngleXU=0 Radius=23.094
    g35: Circle CenterX=-21.6506 CenterY=12.5 CenterZ=0 NormalX=0 NormalY=0 NormalZ=1 AngleXU=0 Radius=1.6
    g36: Circle CenterX=21.6506 CenterY=12.5 CenterZ=0 NormalX=0 NormalY=0 NormalZ=1 AngleXU=0 Radius=1.6
    g37: Circle CenterX=0 CenterY=-25 CenterZ=0 NormalX=0 NormalY=0 NormalZ=1 AngleXU=0 Radius=1.6
    g38: LineSegment [constr] StartX=0 StartY=-25 StartZ=0 EndX=-1e-16 EndY=0 EndZ=0
    g39: LineSegment [constr] StartX=-1e-16 StartY=1e-16 StartZ=0 EndX=21.6506 EndY=12.5 EndZ=0
    g40: LineSegment [constr] StartX=-1e-16 StartY=1e-16 StartZ=0 EndX=-21.6506 EndY=12.5 EndZ=0
    g41: LineSegment [constr] StartX=-45 StartY=126 StartZ=0 EndX=-131.619 EndY=-24.0289 EndZ=0
    g42: LineSegment [constr] StartX=-86.6192 StartY=-101.971 StartZ=0 EndX=86.6192 EndY=-101.971 EndZ=0
    g43: LineSegment [constr] StartX=131.619 StartY=-24.0289 StartZ=0 EndX=45 EndY=126 EndZ=0
    g44: LineSegment [constr] StartX=-45 StartY=126 StartZ=0 EndX=-55 EndY=108.679 EndZ=0
    g45: LineSegment [constr] StartX=-55 StartY=108.679 StartZ=0 EndX=-45 EndY=41 EndZ=0
    g46: LineSegment [constr] StartX=-58.007 StartY=18.4711 StartZ=0 EndX=-121.619 EndY=-6.70835 EndZ=0
    g47: LineSegment [constr] StartX=-121.619 StartY=-6.70835 StartZ=0 EndX=-131.619 EndY=-24.0289 EndZ=0
    g48: LineSegment [constr] StartX=-86.6192 StartY=-101.971 StartZ=0 EndX=-66.6192 EndY=-101.971 EndZ=0
    g49: LineSegment [constr] StartX=-66.6192 StartY=-101.971 StartZ=0 EndX=-13.007 EndY=-59.4711 EndZ=0
    g50: LineSegment [constr] StartX=13.007 StartY=-59.4711 StartZ=0 EndX=66.6192 EndY=-101.971 EndZ=0
    g51: LineSegment [constr] StartX=66.6192 StartY=-101.971 StartZ=0 EndX=86.6192 EndY=-101.971 EndZ=0
    g52: LineSegment [constr] StartX=131.619 StartY=-24.0289 StartZ=0 EndX=121.619 EndY=-6.70835 EndZ=0
    g53: LineSegment [constr] StartX=121.619 StartY=-6.70835 StartZ=0 EndX=58.007 EndY=18.4711 EndZ=0
    g54: LineSegment [constr] StartX=45 StartY=41 StartZ=0 EndX=55 EndY=108.679 EndZ=0
    g55: LineSegment [constr] StartX=55 StartY=108.679 StartZ=0 EndX=45 EndY=126 EndZ=0
  constraints (151):
    c: Coincident(g0,g1)
    c: Coincident(g1,g2)
    c: Vertical(g2)
    c: Coincident(g2,g3)
    c: Horizontal(g3)
    c: Coincident(g3,g4)
    c: Vertical(g4)
    c: Coincident(g4,g5)
    c: Coincident(g5,g6)
    c: Coincident(g6,g7)
    c: Coincident(g7,g8)
    c: Coincident(g8,g9)
    c: Horizontal(g9)
    c: Coincident(g9,g10)
    c: Coincident(g10,g11)
    c: Coincident(g11,g0)
    c: Parallel(g8,g6)
    c: Parallel(g10,g0)
    c: Equal(g4,g6)
    c: Equal(g6,g8)
    c: Equal(g8,g10)
    c: Equal(g10,g0)
    c: Equal(g0,g2)
    c: Perpendicular(g6,g7)
    c: Perpendicular(g11,g10)
    c: Coincident(g12,g-1)
    c: PointOnObject(g12,g3)
    c: Vertical(g12)
    c: Coincident(g13,g12)
    c: Coincident(g14,g12)
    c: Symmetric(g6,g7,g14)
    c: Symmetric(g10,g0,g13)
    c: Perpendicular(g13,g11)
    c: Perpendicular(g7,g14)
    c: DistanceX(g3,g3) = 90
    c: Equal(g9,g5)
    c: Equal(g5,g1)
    c: Angle(g14,g12) = 2.0944
    c: Angle(g12,g13) = 2.0944
    c: DistanceY(g12,g2) = 126
    c: DistanceX(g9,g9) = 26.0141
    c: Coincident(g15,g16)
    c: Coincident(g16,g17)
    c: Coincident(g17,g18)
    c: Coincident(g18,g15)
    c: Horizontal(g15)
    c: Vertical(g16)
    c: Vertical(g18)
    c: Symmetric(g16,g17,g12)
    c: DistanceX(g17,g17) = 55
    c: DistanceY(g16,g16) = 65
    c: Coincident(g19,g20)
    c: Coincident(g20,g21)
    c: Coincident(g21,g22)
    c: Coincident(g22,g19)
    c: Coincident(g23,g24)
    c: Coincident(g24,g25)
    c: Coincident(g25,g26)
    c: Coincident(g26,g23)
    c: Equal(g25,g23)
    c: Equal(g23,g19)
    c: Equal(g19,g21)
    c: Equal(g21,g15)
    c: Equal(g22,g20)
    c: Equal(g20,g16)
    c: Equal(g16,g26)
    c: Equal(g26,g24)
    c: Parallel(g24,g13)
    c: Parallel(g22,g14)
    c: Symmetric(g23,g23,g13)
    c: Symmetric(g21,g20,g14)
    c: Coincident(g27,g12)
    c: PointOnObject(g19,g27)
    c: PointOnObject(g24,g27)
    c: PointOnObject(g15,g27)
    c: Equal(g11,g7)
    c: Equal(g7,g3)
    c: Coincident(g28,g29)
    c: Coincident(g29,g30)
    c: Coincident(g30,g31)
    c: Coincident(g31,g32)
    c: Coincident(g32,g33)
    c: Coincident(g33,g28)
    c: Horizontal(g33)
    c: Horizontal(g30)
    c: Equal(g29,g30)
    c: Equal(g30,g31)
    c: Equal(g31,g32)
    c: Equal(g32,g33)
    c: Equal(g33,g28)
    c: Coincident(g34,g12)
    c: PointOnObject(g30,g34)
    c: PointOnObject(g31,g34)
    c: PointOnObject(g32,g34)
    c: PointOnObject(g28,g34)
    c: PointOnObject(g28,g34)
    c: DistanceY(g12,g30) = 20
    c: PointOnObject(g37,g-2)
    c: Equal(g37,g36)
    c: Equal(g36,g35)
    c: Diameter(g35) = 3.2
    c: Coincident(g38,g37)
    c: Coincident(g38,g12)
    c: Coincident(g39,g12)
    c: Coincident(g39,g36)
    c: Coincident(g40,g12)
    c: Coincident(g40,g35)
    c: Perpendicular(g29,g40)
    c: Perpendicular(g31,g39)
    c: Equal(g40,g38)
    c: Equal(g38,g39)
    c: DistanceY(g38,g38) = 25
    c: Coincident(g41,g3)
    c: Coincident(g41,g11)
    c: Coincident(g42,g11)
    c: Coincident(g42,g7)
    c: Coincident(g43,g7)
    c: Coincident(g43,g3)
    c: Coincident(g3,g44)
    c: PointOnObject(g44,g41)
    c: Coincident(g44,g45)
    c: Coincident(g45,g1)
    c: Coincident(g1,g46)
    c: PointOnObject(g46,g41)
    c: Coincident(g46,g47)
    c: Coincident(g47,g11)
    c: Coincident(g11,g48)
    c: Horizontal(g48)
    c: Coincident(g48,g49)
    c: Coincident(g49,g9)
    c: Coincident(g9,g50)
    c: PointOnObject(g50,g42)
    c: Coincident(g50,g51)
    c: Coincident(g51,g7)
    c: Coincident(g7,g52)
    c: PointOnObject(g52,g43)
    c: Coincident(g52,g53)
    c: Coincident(g53,g5)
    c: Coincident(g5,g54)
    c: PointOnObject(g54,g43)
    c: Coincident(g54,g55)
    c: Coincident(g55,g3)
    c: Equal(g55,g44)
    c: Equal(g44,g47)
    c: Equal(g47,g48)
    c: Equal(g48,g51)
    c: Equal(g55,g52)
    c: DistanceX(g48,g48) = 20
    c: DistanceY(g16) = 105
    c: DistanceY(g50,g12) = 101.971
    c: DistanceY(g4,g4) = 85
FEATURE [PartDesign::Pad] Pad020
  AddSubType = 0
  AutoTaperInnerAngle = false
  CheckUpToFaceLimits = true
  ClaimChildren = false
  Direction = (0,0,1)
  Fit = 0
  FitJoin = 0
  InnerFit = 0
  InnerFitJoin = 0
  InvalidShape = false
  Length = 5
  Length2 = 100
  Linearize = true
  NewSolid = false
  Profile = -> Sketch032
  Refine = true
  Reversed = true
  Suppress = false
  TaperInnerAngle = 0
  TaperInnerAngleRev = 0
  TreeRank = 0
  Type = 0
  ValidateShape = true
  _ProfileBasedVersion = 1
FEATURE [PartDesign::Fillet] Fillet008
  AddSubType = 0
  Base = -> Pad020 [Edge41,Edge44,Edge37,Edge38,Edge65,Edge62,Edge61,Edge68,Edge49,Edge50,Edge53,Edge56]
  BaseFeature = -> Pad020
  InvalidShape = false
  NewSolid = false
  Radius = 3
  Refine = true
  SupportTransform = false
  Suppress = false
  TreeRank = 0
  ValidateShape = true
FEATURE [PartDesign::Fillet] Fillet009
  AddSubType = 0
  Base = -> Fillet008 [Edge110,Edge99,Edge107,Edge106,Edge102,Edge103]
  BaseFeature = -> Fillet008
  InvalidShape = false
  NewSolid = false
  Radius = 5
  Refine = true
  SupportTransform = false
  Suppress = false
  TreeRank = 0
  ValidateShape = true
FEATURE [PartDesign::Fillet] Fillet010
  AddSubType = 0
  Base = -> Fillet009 [Edge53,Edge57,Edge67,Edge71,Edge77,Edge81]
  BaseFeature = -> Fillet009
  InvalidShape = false
  NewSolid = false
  Radius = 5
  Refine = true
  SupportTransform = false
  Suppress = false
  TreeRank = 0
  ValidateShape = true
FEATURE [Sketcher::SketchObject] Sketch033
  ArcFitTolerance = 0
  AttachmentSupport = -> [XY_Plane026]
  ExternalBSplineMaxDegree = 0
  ExternalBSplineTolerance = 0
  FullyConstrained = true
  InternalTolerance = 1e-06
  InvalidShape = false
  MakeInternals = false
  MapMode = 5
  Support = -> [XY_Plane026]
  TreeRank = 0
  ValidateShape = true
  sketch-geometry (13):
    g0: Circle CenterX=-20 CenterY=115 CenterZ=0 NormalX=0 NormalY=0 NormalZ=1 AngleXU=0 Radius=1.75
    g1: Circle CenterX=20 CenterY=115 CenterZ=0 NormalX=0 NormalY=0 NormalZ=1 AngleXU=0 Radius=1.75
    g2: Circle CenterX=-35 CenterY=60 CenterZ=0 NormalX=0 NormalY=0 NormalZ=1 AngleXU=0 Radius=1.75
    g3: Circle CenterX=-35 CenterY=100 CenterZ=0 NormalX=0 NormalY=0 NormalZ=1 AngleXU=0 Radius=1.75
    g4: Circle CenterX=35 CenterY=100 CenterZ=0 NormalX=0 NormalY=0 NormalZ=1 AngleXU=0 Radius=1.75
    g5: Circle CenterX=35 CenterY=60 CenterZ=0 NormalX=0 NormalY=0 NormalZ=1 AngleXU=0 Radius=1.75
    g6: Circle CenterX=-35 CenterY=115 CenterZ=0 NormalX=0 NormalY=0 NormalZ=1 AngleXU=0 Radius=3.1
    g7: Circle CenterX=35 CenterY=115 CenterZ=0 NormalX=0 NormalY=0 NormalZ=1 AngleXU=0 Radius=3.1
    g8: Circle CenterX=-35 CenterY=80 CenterZ=0 NormalX=0 NormalY=0 NormalZ=1 AngleXU=0 Radius=2.2
    g9: Circle CenterX=35 CenterY=80 CenterZ=0 NormalX=0 NormalY=0 NormalZ=1 AngleXU=0 Radius=2.2
    g10: Circle CenterX=-35 CenterY=50 CenterZ=0 NormalX=0 NormalY=0 NormalZ=1 AngleXU=0 Radius=2.2
    g11: Circle CenterX=35 CenterY=50 CenterZ=0 NormalX=0 NormalY=0 NormalZ=1 AngleXU=0 Radius=2.2
    g12: Circle CenterX=-1.0206e-12 CenterY=115 CenterZ=0 NormalX=0 NormalY=0 NormalZ=1 AngleXU=0 Radius=2.2
  constraints (31):
    c: Equal(g0,g3)
    c: Equal(g3,g2)
    c: Equal(g2,g1)
    c: Equal(g1,g4)
    c: Equal(g4,g5)
    c: Diameter(g0) = 3.5
    c: Symmetric(g1,g0,g-2)
    c: Symmetric(g3,g4,g-2)
    c: Symmetric(g2,g5,g-2)
    c: Vertical(g3,g2)
    c: DistanceX(g3,g4) = 70
    c: DistanceX(g0,g1) = 40
    c: DistanceY(g4,g1) = 15
    c: DistanceY(g5,g4) = 40
    c: DistanceY(g-1,g1) = 115
    c: Symmetric(g7,g6,g-2)
    c: Horizontal(g6,g0)
    c: Diameter(g7) = 6.2
    c: Equal(g7,g6)
    c: Vertical(g7,g4)
    c: Equal(g9,g8)
    c: Symmetric(g8,g9,g-2)
    c: Symmetric(g5,g4,g9)
    c: Diameter(g9) = 4.4
    c: Symmetric(g1,g0,g12)
    c: Equal(g12,g11)
    c: Equal(g11,g10)
    c: Equal(g10,g9)
    c: Vertical(g11,g5)
    c: Symmetric(g11,g10,g-2)
    c: DistanceY(g11,g5) = 10
FEATURE [PartDesign::Pocket] Pocket012
  AddSubType = 1
  AutoTaperInnerAngle = false
  BaseFeature = -> Fillet010
  CheckUpToFaceLimits = true
  ClaimChildren = false
  Fit = 0
  FitJoin = 0
  InnerFit = 0
  InnerFitJoin = 0
  InvalidShape = false
  Length = 5
  Length2 = 100
  Linearize = true
  NewSolid = false
  Profile = -> Sketch033
  Refine = true
  Suppress = false
  TaperInnerAngle = 0
  TaperInnerAngleRev = 0
  TreeRank = 0
  Type = 1
  ValidateShape = true
  _ProfileBasedVersion = 1
  _Version = 0
FEATURE [PartDesign::PolarPattern] PolarPattern013
  AddSubType = 0
  Angle = 360
  Axis = -> Sketch033 [N_Axis]
  BaseFeature = -> Pocket012
  CopyShape = false
  InvalidShape = false
  NewSolid = false
  Occurrences = 3
  OriginalSubs = -> [Pocket012]
  Originals = -> [Pocket012]
  ParallelTransform = true
  Refine = true
  SubTransform = true
  Suppress = false
  TreeRank = 0
  ValidateShape = true
  _Version = 0
FEATURE [PartDesign::Fillet] Fillet011
  AddSubType = 0
  Base = -> PolarPattern013 [Edge190,Edge189,Edge192,Edge196,Edge198,Edge194]
  BaseFeature = -> PolarPattern013
  InvalidShape = false
  NewSolid = false
  Radius = 3
  Refine = true
  SupportTransform = false
  Suppress = false
  TreeRank = 0
  ValidateShape = true
FEATURE [PartDesign::Body] Body019  label="Semelle"
  AutoGroupSolids = false
  ClaimAllChildren = false
  ExportMode = 0
  Group = -> [Sketch032,Pad020,Fillet008,Fillet009,Fillet010,Sketch033,Pocket012,PolarPattern013,Fillet011]
  InvalidShape = false
  Origin = -> Origin029
  SingleSolid = true
  Tip = -> Fillet011
  TreeRank = 0
  ValidateShape = true
  _ExportChildren = -> [Pad020,Fillet008,Fillet009,Fillet010,Pocket012,PolarPattern013,Fillet011]
  _GroupVersion = 1
FEATURE [Sketcher::SketchObject] Sketch034
  ArcFitTolerance = 0
  AttachmentSupport = -> [XY_Plane027]
  ExternalBSplineMaxDegree = 0
  ExternalBSplineTolerance = 0
  FullyConstrained = true
  InternalTolerance = 1e-06
  InvalidShape = false
  MakeInternals = false
  MapMode = 5
  Support = -> [XY_Plane027]
  TreeRank = 0
  ValidateShape = true
  sketch-geometry (33):
    g0: LineSegment StartX=-54.641 StartY=14.641 StartZ=0 EndX=-40 EndY=40 EndZ=0
    g1: LineSegment StartX=-40 StartY=40 StartZ=0 EndX=-31 EndY=40 EndZ=0
    g2: LineSegment StartX=-31 StartY=40 StartZ=0 EndX=-31 EndY=34 EndZ=0
    g3: LineSegment StartX=-31 StartY=34 StartZ=0 EndX=31 EndY=34 EndZ=0
    g4: LineSegment StartX=31 StartY=34 StartZ=0 EndX=31 EndY=40 EndZ=0
    g5: LineSegment StartX=31 StartY=40 StartZ=0 EndX=40 EndY=40 EndZ=0
    g6: LineSegment StartX=40 StartY=40 StartZ=0 EndX=54.641 EndY=14.641 EndZ=0
    g7: LineSegment StartX=54.641 StartY=14.641 StartZ=0 EndX=50.141 EndY=6.84679 EndZ=0
    g8: LineSegment StartX=50.141 StartY=6.84679 StartZ=0 EndX=44.9449 EndY=9.84679 EndZ=0
    g9: LineSegment StartX=44.9449 StartY=9.84679 StartZ=0 EndX=13.9449 EndY=-43.8468 EndZ=0
    g10: LineSegment StartX=13.9449 StartY=-43.8468 StartZ=0 EndX=19.141 EndY=-46.8468 EndZ=0
    g11: LineSegment StartX=19.141 StartY=-46.8468 StartZ=0 EndX=14.641 EndY=-54.641 EndZ=0
    g12: LineSegment StartX=14.641 StartY=-54.641 StartZ=0 EndX=-14.641 EndY=-54.641 EndZ=0
    g13: LineSegment StartX=-14.641 StartY=-54.641 StartZ=0 EndX=-19.141 EndY=-46.8468 EndZ=0
    g14: LineSegment StartX=-19.141 StartY=-46.8468 StartZ=0 EndX=-13.9449 EndY=-43.8468 EndZ=0
    g15: LineSegment StartX=-13.9449 StartY=-43.8468 StartZ=0 EndX=-44.9449 EndY=9.84679 EndZ=0
    g16: LineSegment StartX=-44.9449 StartY=9.84679 StartZ=0 EndX=-50.141 EndY=6.84679 EndZ=0
    g17: LineSegment StartX=-50.141 StartY=6.84679 StartZ=0 EndX=-54.641 EndY=14.641 EndZ=0
    g18: Circle [constr] CenterX=0 CenterY=0 CenterZ=0 NormalX=0 NormalY=0 NormalZ=1 AngleXU=0 Radius=56.5685
    g19: Circle [constr] CenterX=0 CenterY=0 CenterZ=0 NormalX=0 NormalY=0 NormalZ=1 AngleXU=0 Radius=25
    g20: Circle CenterX=-21.6506 CenterY=12.5 CenterZ=0 NormalX=0 NormalY=0 NormalZ=1 AngleXU=0 Radius=1.6
    g21: Circle CenterX=21.6506 CenterY=12.5 CenterZ=0 NormalX=0 NormalY=0 NormalZ=1 AngleXU=0 Radius=1.6
    g22: Circle CenterX=0 CenterY=-25 CenterZ=0 NormalX=0 NormalY=0 NormalZ=1 AngleXU=0 Radius=1.6
    g23: LineSegment [constr] StartX=0 StartY=0 StartZ=0 EndX=21.6506 EndY=12.5 EndZ=0
    g24: LineSegment [constr] StartX=0 StartY=0 StartZ=0 EndX=0 EndY=-25 EndZ=0
    g25: LineSegment [constr] StartX=0 StartY=0 StartZ=0 EndX=-21.6506 EndY=12.5 EndZ=0
    g26: LineSegment StartX=11.547 StartY=20 StartZ=0 EndX=-11.547 EndY=20 EndZ=0
    g27: LineSegment StartX=-11.547 StartY=20 StartZ=0 EndX=-23.094 EndY=1.0409e-12 EndZ=0
    g28: LineSegment StartX=-23.094 StartY=1.0409e-12 StartZ=0 EndX=-11.547 EndY=-20 EndZ=0
    g29: LineSegment StartX=-11.547 StartY=-20 StartZ=0 EndX=11.547 EndY=-20 EndZ=0
    g30: LineSegment StartX=11.547 StartY=-20 StartZ=0 EndX=23.094 EndY=1.0374e-12 EndZ=0
    g31: LineSegment StartX=23.094 StartY=1.0374e-12 StartZ=0 EndX=11.547 EndY=20 EndZ=0
    g32: Circle [constr] CenterX=0 CenterY=0 CenterZ=0 NormalX=0 NormalY=0 NormalZ=1 AngleXU=0 Radius=23.094
  constraints (88):
    c: Coincident(g0,g1)
    c: Horizontal(g1)
    c: Coincident(g1,g2)
    c: Vertical(g2)
    c: Coincident(g2,g3)
    c: Coincident(g3,g4)
    c: Vertical(g4)
    c: Coincident(g4,g5)
    c: Horizontal(g5)
    c: Coincident(g5,g6)
    c: Coincident(g6,g7)
    c: Coincident(g7,g8)
    c: Coincident(g8,g9)
    c: Coincident(g9,g10)
    c: Coincident(g10,g11)
    c: Coincident(g11,g12)
    c: Horizontal(g12)
    c: Coincident(g12,g13)
    c: Coincident(g13,g14)
    c: Coincident(g14,g15)
    c: Coincident(g15,g16)
    c: Coincident(g16,g17)
    c: Coincident(g17,g0)
    c: DistanceY(g-1,g1) = 40
    c: DistanceX(g1,g1) = 9
    c: Equal(g5,g1)
    c: Equal(g1,g17)
    c: Equal(g17,g13)
    c: Equal(g13,g11)
    c: Equal(g11,g7)
    c: Perpendicular(g10,g11)
    c: Perpendicular(g14,g13)
    c: Perpendicular(g15,g14)
    c: Perpendicular(g9,g10)
    c: Perpendicular(g9,g8)
    c: Perpendicular(g8,g7)
    c: Perpendicular(g17,g16)
    c: Perpendicular(g15,g16)
    c: DistanceY(g2,g2) = 6
    c: Equal(g8,g4)
    c: Equal(g4,g16)
    c: Equal(g0,g6)
    c: Equal(g6,g12)
    c: Coincident(g18,g-1)
    c: PointOnObject(g5,g18)
    c: PointOnObject(g6,g18)
    c: PointOnObject(g11,g18)
    c: PointOnObject(g12,g18)
    c: PointOnObject(g0,g18)
    c: PointOnObject(g0,g18)
    c: Symmetric(g3,g2,g-2)
    c: DistanceX(g3,g3) = 62
    c: Angle(g15,g3) = 1.0472
    c: Angle(g3,g9) = 1.0472
    c: Equal(g10,g8)
    c: Coincident(g19,g18)
    c: PointOnObject(g20,g19)
    c: PointOnObject(g21,g19)
    c: PointOnObject(g22,g19)
    c: PointOnObject(g22,g-2)
    c: Coincident(g23,g18)
    c: Coincident(g23,g21)
    c: Coincident(g24,g18)
    c: Coincident(g24,g22)
    c: Coincident(g25,g18)
    c: Coincident(g25,g20)
    c: Angle(g23,g25) = 2.0944
    c: Angle(g24,g23) = 2.0944
    c: DistanceY(g24,g24) = 25
    c: Equal(g21,g22)
    c: Equal(g22,g20)
    c: Diameter(g21) = 3.2
    c: Coincident(g26,g27)
    c: Coincident(g27,g28)
    c: Coincident(g28,g29)
    c: Coincident(g29,g30)
    c: Coincident(g30,g31)
    c: Coincident(g31,g26)
    c: Equal(g26, g27-g31) x5
    c: PointOnObject(g26,g32)
    c: PointOnObject(g27,g32)
    c: PointOnObject(g28,g32)
    c: PointOnObject(g29,g32)
    c: PointOnObject(g30,g32)
    c: PointOnObject(g31,g32)
    c: Coincident(g32,g18)
    c: Horizontal(g26)
    c: DistanceY(g26) = 20
FEATURE [PartDesign::Pad] Pad021
  AddSubType = 0
  AutoTaperInnerAngle = false
  CheckUpToFaceLimits = true
  ClaimChildren = false
  Direction = (1,1,1)
  Fit = 0
  FitJoin = 0
  InnerFit = 0
  InnerFitJoin = 0
  InvalidShape = false
  Length = 5
  Length2 = 100
  Linearize = true
  NewSolid = false
  Profile = -> Sketch034
  Refine = true
  Suppress = false
  TaperInnerAngle = 0
  TaperInnerAngleRev = 0
  TreeRank = 0
  Type = 0
  ValidateShape = true
  _ProfileBasedVersion = 1
FEATURE [PartDesign::Fillet] Fillet012
  AddSubType = 0
  Base = -> Pad021 [Edge59,Edge56,Edge68,Edge55,Edge65,Edge62]
  BaseFeature = -> Pad021
  InvalidShape = false
  NewSolid = false
  Radius = 3
  Refine = true
  SupportTransform = false
  Suppress = false
  TreeRank = 0
  ValidateShape = true
FEATURE [PartDesign::Fillet] Fillet013
  AddSubType = 0
  Base = -> Fillet012 [Edge94,Edge93,Edge95,Edge96,Edge81,Edge82,Edge84,Edge83,Edge88,Edge87,Edge86,Edge85,Edge80,Edge79,Edge92,Edge91,Edge90,Edge89]
  BaseFeature = -> Fillet012
  InvalidShape = false
  NewSolid = false
  Radius = 0.5
  Refine = true
  SupportTransform = false
  Suppress = false
  TreeRank = 0
  ValidateShape = true
FEATURE [PartDesign::Body] Body020  label="CaleCentrale"
  AutoGroupSolids = false
  ClaimAllChildren = false
  ExportMode = 0
  Group = -> [Sketch034,Pad021,Fillet012,Fillet013]
  InvalidShape = false
  Origin = -> Origin030
  SingleSolid = true
  Tip = -> Fillet013
  TreeRank = 0
  ValidateShape = true
  _ExportChildren = -> [Pad021,Fillet012,Fillet013]
  _GroupVersion = 1
COMPONENT P8 — recipe-attached ("SupportGauche120d", modeled in this document).
Construction recipe (the document's own serialized feature program — sketch geometry with constraints, then the solid features built on it; lengths are millimeters unless a unit is written):

FEATURE [Sketcher::SketchObject] Sketch049
  ArcFitTolerance = 0
  AttachmentSupport = -> [XY_Plane033]
  ExternalBSplineMaxDegree = 0
  ExternalBSplineTolerance = 0
  FullyConstrained = true
  InternalTolerance = 1e-06
  InvalidShape = false
  MakeInternals = false
  MapMode = 5
  Support = -> [XY_Plane033]
  TreeRank = 0
  ValidateShape = true
  sketch-geometry (13):
    g0: LineSegment [constr] StartX=0 StartY=0 StartZ=0 EndX=0 EndY=12.5 EndZ=0
    g1: LineSegment StartX=0 StartY=12.5 StartZ=0 EndX=5 EndY=21.1603 EndZ=0
    g2: LineSegment StartX=5 StartY=21.1603 StartZ=0 EndX=13.6603 EndY=16.1603 EndZ=0
    g3: LineSegment StartX=13.6603 StartY=16.1603 StartZ=0 EndX=4.33013 EndY=0 EndZ=0
    g4: LineSegment StartX=4.33013 StartY=0 StartZ=0 EndX=0 EndY=0 EndZ=0
    g5: LineSegment StartX=0 StartY=12.5 StartZ=0 EndX=-2 EndY=12.5 EndZ=0
    g6: LineSegment StartX=-2 StartY=12.5 StartZ=0 EndX=-2 EndY=10 EndZ=0
    g7: LineSegment StartX=-2 StartY=10 StartZ=0 EndX=0 EndY=10 EndZ=0
    g8: LineSegment StartX=0 StartY=10 StartZ=0 EndX=0 EndY=6.25 EndZ=0
    g9: LineSegment StartX=0 StartY=6.25 StartZ=0 EndX=-2 EndY=6.25 EndZ=0
    g10: LineSegment StartX=-2 StartY=6.25 StartZ=0 EndX=-2 EndY=3.75 EndZ=0
    g11: LineSegment StartX=-2 StartY=3.75 StartZ=0 EndX=0 EndY=3.75 EndZ=0
    g12: LineSegment StartX=0 StartY=3.75 StartZ=0 EndX=0 EndY=0 EndZ=0
  constraints (37):
    c: Coincident(g-1,g0)
    c: PointOnObject(g0,g-2)
    c: Coincident(g1,g2)
    c: Coincident(g2,g3)
    c: PointOnObject(g3,g-1)
    c: Coincident(g3,g4)
    c: Coincident(g4,g0)
    c: Perpendicular(g2,g1)
    c: Perpendicular(g2,g3)
    c: DistanceY(g0,g0) = 12.5
    c: Distance(g2) = 10
    c: Distance(g1) = 10
    c: Horizontal(g5)
    c: Coincident(g6,g5)
    c: Vertical(g6)
    c: Coincident(g7,g6)
    c: PointOnObject(g7,g0)
    c: Horizontal(g7)
    c: Coincident(g8,g7)
    c: PointOnObject(g8,g0)
    c: Coincident(g9,g8)
    c: Coincident(g10,g9)
    c: Coincident(g11,g10)
    c: PointOnObject(g11,g0)
    c: Coincident(g12,g11)
    c: Coincident(g12,g4)
    c: Perpendicular(g10,g9)
    c: Perpendicular(g10,g11)
    c: Parallel(g10,g8)
    c: Equal(g8,g12)
    c: DistanceY(g4,g7) = 10
    c: DistanceY(g10,g10) = 2.5
    c: DistanceX(g9,g9) = 2
    c: DistanceX(g5,g5) = 2
    c: Coincident(g1,g5)
    c: Coincident(g1,g0)
    c: Angle(g1,g5) = 2.0944
FEATURE [PartDesign::Pad] Pad029
  AddSubType = 0
  AutoTaperInnerAngle = false
  CheckUpToFaceLimits = true
  ClaimChildren = false
  Direction = (1,1,1)
  Fit = 0
  FitJoin = 0
  InnerFit = 0
  InnerFitJoin = 0
  InvalidShape = false
  Length = 7
  Length2 = 100
  Linearize = true
  NewSolid = false
  Profile = -> Sketch049
  Refine = true
  Suppress = false
  TaperInnerAngle = 0
  TaperInnerAngleRev = 0
  TreeRank = 0
  Type = 0
  ValidateShape = true
  _ProfileBasedVersion = 1
FEATURE [Sketcher::SketchObject] Sketch051
  ArcFitTolerance = 0
  AttachmentSupport = -> [XY_Plane033]
  ExternalBSplineMaxDegree = 0
  ExternalBSplineTolerance = 0
  ExternalGeometry = -> [Pad029]
  FullyConstrained = true
  InternalTolerance = 1e-06
  InvalidShape = false
  MakeInternals = false
  MapMode = 5
  Support = -> [XY_Plane033]
  TreeRank = 0
  ValidateShape = true
  sketch-geometry (4):
    g0: LineSegment StartX=4.33013 StartY=10 StartZ=0 EndX=4.33013 EndY=0 EndZ=0
    g1: LineSegment StartX=0 StartY=6.25 StartZ=0 EndX=0 EndY=3.75 EndZ=0
    g2: LineSegment StartX=4.33013 StartY=10 StartZ=0 EndX=0 EndY=12.5 EndZ=0
    g3: LineSegment StartX=0 StartY=12.5 StartZ=0 EndX=-2 EndY=12.5 EndZ=0
  constraints (10):
    c: Vertical(g0)
    c: Coincident(g1,g-8)
    c: Coincident(g1,g-5)
    c: Coincident(g0,g-11)
    c: Coincident(g2,g0)
    c: PointOnObject(g2,g-12)
    c: Coincident(g3,g-10)
    c: Coincident(g2,g3)
    c: Horizontal(g3)
    c: Perpendicular(g-12,g2)
FEATURE [PartDesign::Pad] Pad030
  AddSubType = 0
  AutoTaperInnerAngle = false
  BaseFeature = -> Pad029
  CheckUpToFaceLimits = true
  ClaimChildren = false
  Direction = (1,1,1)
  Fit = 0
  FitJoin = 0
  InnerFit = 0
  InnerFitJoin = 0
  InvalidShape = false
  Length = 15
  Length2 = 100
  Linearize = true
  NewSolid = false
  Profile = -> Sketch051
  Refine = true
  Reversed = true
  Suppress = false
  TaperInnerAngle = 0
  TaperInnerAngleRev = 0
  TreeRank = 0
  Type = 0
  ValidateShape = true
  _ProfileBasedVersion = 1
FEATURE [Sketcher::SketchObject] Sketch052
  ArcFitTolerance = 0
  AttachmentSupport = -> [YZ_Plane033]
  ExternalBSplineMaxDegree = 0
  ExternalBSplineTolerance = 0
  ExternalGeometry = -> [Pad030]
  FullyConstrained = true
  InternalTolerance = 1e-06
  InvalidShape = false
  MakeInternals = false
  MapMode = 5
  Placement = pos=(0,0,0) rot=(0.57735,0.57735,0.57735;2.0944rad)
  Support = -> [YZ_Plane033]
  TreeRank = 0
  ValidateShape = true
  sketch-geometry (1):
    g0: Circle CenterX=5 CenterY=-10 CenterZ=0 NormalX=0 NormalY=0 NormalZ=1 AngleXU=0 Radius=1.6
  constraints (3):
    c: DistanceX(g0) = 5
    c: Diameter(g0) = 3.2
    c: DistanceY(g-3,g0) = 5
FEATURE [PartDesign::Pocket] Pocket020
  AddSubType = 1
  AutoTaperInnerAngle = false
  BaseFeature = -> Pad030
  CheckUpToFaceLimits = true
  ClaimChildren = false
  Fit = 0
  FitJoin = 0
  InnerFit = 0
  InnerFitJoin = 0
  InvalidShape = false
  Length = 5
  Length2 = 100
  Linearize = true
  NewSolid = false
  Profile = -> Sketch052
  Refine = true
  Reversed = true
  Suppress = false
  TaperInnerAngle = 0
  TaperInnerAngleRev = 0
  TreeRank = 0
  Type = 1
  ValidateShape = true
  _ProfileBasedVersion = 1
  _Version = 0
FEATURE [Sketcher::SketchObject] Sketch054
  ArcFitTolerance = 0
  AttachmentSupport = -> [XY_Plane033]
  ExternalBSplineMaxDegree = 0
  ExternalBSplineTolerance = 0
  ExternalGeometry = -> [Pocket020]
  FullyConstrained = true
  InternalTolerance = 1e-06
  InvalidShape = false
  MakeInternals = false
  MapMode = 5
  Support = -> [XY_Plane033]
  TreeRank = 0
  ValidateShape = true
  sketch-geometry (3):
    g0: Circle CenterX=6.83013 CenterY=14.3301 CenterZ=0 NormalX=0 NormalY=0 NormalZ=1 AngleXU=0 Radius=2.1
    g1: LineSegment [constr] StartX=9.33013 StartY=18.6603 StartZ=0 EndX=6.83013 EndY=14.3301 EndZ=0
    g2: LineSegment [constr] StartX=6.83013 StartY=14.3301 StartZ=0 EndX=11.1603 EndY=11.8301 EndZ=0
  constraints (11):
    c: Diameter(g0) = 4.2
    c: Coincident(g1,g0)
    c: Coincident(g1,g2)
    c: Perpendicular(g1,g2)
    c: Distance(g1) = 5
    c: Distance(g2) = 5
    c: PointOnObject(g2,g-4)
    c: PointOnObject(g1,g-3)
    c: Perpendicular(g-3,g1)
    c: DistanceX(g-1,g0) = 6.83013
    c: DistanceY(g-1,g0) = 14.3301
FEATURE [PartDesign::Pocket] Pocket022
  AddSubType = 1
  AutoTaperInnerAngle = false
  BaseFeature = -> Pocket020
  CheckUpToFaceLimits = true
  ClaimChildren = false
  Fit = 0
  FitJoin = 0
  InnerFit = 0
  InnerFitJoin = 0
  InvalidShape = false
  Length = 5
  Length2 = 100
  Linearize = true
  NewSolid = false
  Profile = -> Sketch054
  Refine = true
  Reversed = true
  Suppress = false
  TaperInnerAngle = 0
  TaperInnerAngleRev = 0
  TreeRank = 0
  Type = 1
  ValidateShape = true
  _ProfileBasedVersion = 1
  _Version = 0
FEATURE [Sketcher::SketchObject] Sketch055
  ArcFitTolerance = 0
  AttachmentSupport = -> [Pocket022]
  ExternalBSplineMaxDegree = 0
  ExternalBSplineTolerance = 0
  ExternalGeometry = -> [Pocket022]
  FullyConstrained = true
  InternalTolerance = 1e-06
  InvalidShape = false
  MakeInternals = false
  MapMode = 5
  Placement = pos=(4.33013,0,0) rot=(0.57735,0.57735,0.57735;2.0944rad)
  Support = -> [Pocket022]
  TreeRank = 0
  ValidateShape = true
  sketch-geometry (4):
    g0: LineSegment StartX=0 StartY=-15 StartZ=0 EndX=12.5 EndY=-15 EndZ=0
    g1: LineSegment StartX=12.5 StartY=-15 StartZ=0 EndX=12.5 EndY=-5 EndZ=0
    g2: LineSegment StartX=12.5 StartY=-5 StartZ=0 EndX=0 EndY=-5 EndZ=0
    g3: LineSegment StartX=0 StartY=-5 StartZ=0 EndX=0 EndY=-15 EndZ=0
  constraints (11):
    c: Coincident(g0,g1)
    c: Coincident(g1,g2)
    c: Coincident(g2,g3)
    c: Coincident(g3,g0)
    c: Horizontal(g0)
    c: Horizontal(g2)
    c: Vertical(g1)
    c: Vertical(g3)
    c: PointOnObject(g1,g-4)
    c: Coincident(g0,g-3)
    c: DistanceY(g3,g3) = 10
FEATURE [PartDesign::Pocket] Pocket023
  AddSubType = 1
  AutoTaperInnerAngle = false
  BaseFeature = -> Pocket022
  CheckUpToFaceLimits = true
  ClaimChildren = false
  Fit = 0
  FitJoin = 0
  InnerFit = 0
  InnerFitJoin = 0
  InvalidShape = false
  Length = 1.9
  Length2 = 100
  Linearize = true
  NewSolid = false
  Profile = -> Sketch055
  Refine = true
  Suppress = false
  TaperInnerAngle = 0
  TaperInnerAngleRev = 0
  TreeRank = 0
  Type = 0
  ValidateShape = true
  _ProfileBasedVersion = 1
  _Version = 0
FEATURE [Sketcher::SketchObject] Sketch056
  ArcFitTolerance = 0
  AttachmentSupport = -> [XY_Plane033]
  ExternalBSplineMaxDegree = 0
  ExternalBSplineTolerance = 0
  ExternalGeometry = -> [Pocket023]
  FullyConstrained = true
  InternalTolerance = 1e-06
  InvalidShape = false
  MakeInternals = false
  MapMode = 5
  Support = -> [XY_Plane033]
  TreeRank = 0
  ValidateShape = true
  sketch-geometry (3):
    g0: LineSegment StartX=4.33013 StartY=10 StartZ=0 EndX=4.33013 EndY=0 EndZ=0
    g1: LineSegment StartX=4.33013 StartY=0 StartZ=0 EndX=8.66025 EndY=7.5 EndZ=0
    g2: LineSegment StartX=8.66025 StartY=7.5 StartZ=0 EndX=4.33013 EndY=10 EndZ=0
  constraints (7):
    c: Coincident(g-5,g0)
    c: Coincident(g0,g-4)
    c: Coincident(g0,g1)
    c: PointOnObject(g1,g-4)
    c: Coincident(g1,g2)
    c: Coincident(g2,g0)
    c: Parallel(g2,g-5)
FEATURE [PartDesign::Pad] Pad031
  AddSubType = 0
  AutoTaperInnerAngle = false
  BaseFeature = -> Pocket023
  CheckUpToFaceLimits = true
  ClaimChildren = false
  Direction = (1,1,1)
  Fit = 0
  FitJoin = 0
  InnerFit = 0
  InnerFitJoin = 0
  InvalidShape = false
  Length = 10
  Length2 = 100
  Linearize = true
  NewSolid = false
  Profile = -> Sketch056
  Refine = true
  Reversed = true
  Suppress = false
  TaperInnerAngle = 0
  TaperInnerAngleRev = 0
  TreeRank = 0
  Type = 3
  UpToFace = -> Pocket023 [Face19]
  ValidateShape = true
  _ProfileBasedVersion = 1
FEATURE [PartDesign::Draft] Draft
  AddSubType = 0
  Angle = 38.5
  Base = -> Pad031 [Face20]
  BaseFeature = -> Pad031
  InvalidShape = false
  NeutralPlane = -> Pad031 [Face15]
  NewSolid = false
  Refine = true
  SupportTransform = false
  Suppress = false
  TreeRank = 0
  ValidateShape = true
FEATURE [PartDesign::Chamfer] Chamfer009
  AddSubType = 0
  Angle = 45
  Base = -> Draft [Edge26]
  BaseFeature = -> Draft
  ChamferType = 0
  FlipDirection = false
  InvalidShape = false
  NewSolid = false
  Refine = true
  Size = 2
  Size2 = 1
  SupportTransform = false
  Suppress = false
  TreeRank = 0
  ValidateShape = true
FEATURE [PartDesign::Draft] Draft001
  AddSubType = 0
  Angle = 66.5
  Base = -> Chamfer009 [Face16]
  BaseFeature = -> Chamfer009
  InvalidShape = false
  NeutralPlane = -> Chamfer009 [Face21]
  NewSolid = false
  Refine = true
  Reversed = true
  SupportTransform = false
  Suppress = false
  TreeRank = 0
  ValidateShape = true
FEATURE [PartDesign::Chamfer] Chamfer010
  AddSubType = 0
  Angle = 45
  Base = -> Draft001 [Edge51,Edge50,Edge54,Edge53]
  BaseFeature = -> Draft001
  ChamferType = 0
  FlipDirection = false
  InvalidShape = false
  NewSolid = false
  Refine = true
  Size = 0.4
  Size2 = 1
  SupportTransform = false
  Suppress = false
  TreeRank = 0
  ValidateShape = true
FEATURE [PartDesign::Chamfer] Chamfer011
  AddSubType = 0
  Angle = 45
  Base = -> Chamfer010 [Edge45]
  BaseFeature = -> Chamfer010
  ChamferType = 0
  FlipDirection = false
  InvalidShape = false
  NewSolid = false
  Refine = true
  Size = 1
  Size2 = 1
  SupportTransform = false
  Suppress = false
  TreeRank = 0
  ValidateShape = true
FEATURE [PartDesign::Chamfer] Chamfer012
  AddSubType = 0
  Angle = 45
  Base = -> Chamfer011 [Edge10,Edge19]
  BaseFeature = -> Chamfer011
  ChamferType = 0
  FlipDirection = false
  InvalidShape = false
  NewSolid = false
  Refine = true
  Size = 0.2
  Size2 = 1
  SupportTransform = false
  Suppress = false
  TreeRank = 0
  ValidateShape = true
FEATURE [PartDesign::Chamfer] Chamfer013
  AddSubType = 0
  Angle = 45
  Base = -> Chamfer012 [Edge64,Edge38]
  BaseFeature = -> Chamfer012
  ChamferType = 0
  FlipDirection = false
  InvalidShape = false
  NewSolid = false
  Refine = true
  Size = 1
  Size2 = 1
  SupportTransform = false
  Suppress = false
  TreeRank = 0
  ValidateShape = true
FEATURE [PartDesign::Fillet] Fillet016
  AddSubType = 0
  Base = -> Chamfer013 [Edge37]
  BaseFeature = -> Chamfer013
  InvalidShape = false
  NewSolid = false
  Radius = 2
  Refine = true
  SupportTransform = false
  Suppress = false
  TreeRank = 0
  ValidateShape = true
FEATURE [PartDesign::Chamfer] Chamfer014
  AddSubType = 0
  Angle = 45
  Base = -> Fillet016 [Edge20,Edge70,Edge79,Edge44]
  BaseFeature = -> Fillet016
  ChamferType = 0
  FlipDirection = false
  InvalidShape = false
  NewSolid = false
  Refine = true
  Size = 0.2
  Size2 = 1
  SupportTransform = false
  Suppress = false
  TreeRank = 0
  ValidateShape = true
FEATURE [Sketcher::SketchObject] Sketch057
  ArcFitTolerance = 0
  AttachmentSupport = -> [XY_Plane033]
  ExternalBSplineMaxDegree = 0
  ExternalBSplineTolerance = 0
  FullyConstrained = false
  InternalTolerance = 1e-06
  InvalidShape = false
  MakeInternals = false
  MapMode = 5
  Support = -> [XY_Plane033]
  TreeRank = 0
  ValidateShape = true
  sketch-geometry (4):
    g0: LineSegment StartX=0 StartY=15.6465 StartZ=0 EndX=-3.55109 EndY=15.6465 EndZ=0
    g1: LineSegment StartX=-3.55109 StartY=15.6465 StartZ=0 EndX=-3.55109 EndY=7.42705 EndZ=0
    g2: LineSegment StartX=-3.55109 StartY=7.42705 StartZ=0 EndX=0 EndY=7.42705 EndZ=0
    g3: LineSegment StartX=0 StartY=7.42705 StartZ=0 EndX=0 EndY=15.6465 EndZ=0
  constraints (9):
    c: Coincident(g0,g1)
    c: Coincident(g1,g2)
    c: Coincident(g2,g3)
    c: Coincident(g3,g0)
    c: Horizontal(g0)
    c: Horizontal(g2)
    c: Vertical(g1)
    c: Vertical(g3)
    c: PointOnObject(g0,g-2)
FEATURE [PartDesign::Pocket] Pocket024
  AddSubType = 1
  AutoTaperInnerAngle = false
  BaseFeature = -> Chamfer014
  CheckUpToFaceLimits = true
  ClaimChildren = false
  Fit = 0
  FitJoin = 0
  InnerFit = 0
  InnerFitJoin = 0
  InvalidShape = false
  Length = 39
  Length2 = 100
  Linearize = true
  Midplane = true
  NewSolid = false
  Profile = -> Sketch057
  Refine = true
  Suppress = false
  TaperInnerAngle = 0
  TaperInnerAngleRev = 0
  TreeRank = 0
  Type = 1
  ValidateShape = true
  _ProfileBasedVersion = 1
  _Version = 0
FEATURE [PartDesign::Chamfer] Chamfer015
  AddSubType = 0
  Angle = 45
  Base = -> Pocket024 [Edge69,Edge58,Edge54]
  BaseFeature = -> Pocket024
  ChamferType = 0
  FlipDirection = false
  InvalidShape = false
  NewSolid = false
  Refine = true
  Size = 0.5
  Size2 = 1
  SupportTransform = false
  Suppress = false
  TreeRank = 0
  ValidateShape = true
FEATURE [PartDesign::Body] Body026
  AutoGroupSolids = false
  ClaimAllChildren = false
  ExportMode = 0
  Group = -> [Sketch049,Sketch051,Sketch052,Sketch054,Pad029,Pad030,Pocket020,Pocket022,Sketch055,Pocket023,Sketch056,Pad031,Draft,Chamfer009,Draft001,Chamfer010,Chamfer011,Chamfer012,Chamfer013,Fillet016,Chamfer014,Sketch057,Pocket024,Chamfer015]
  InvalidShape = false
  Origin = -> Origin041
  SingleSolid = true
  Tip = -> Chamfer015
  TreeRank = 0
  ValidateShape = true
  _ExportChildren = -> [Pad029,Pad030,Pocket020,Pocket022,Pocket023,Pad031,Draft,Chamfer009,Draft001,Chamfer010,Chamfer011,Chamfer012,Chamfer013,Fillet016,Chamfer014,Pocket024,Chamfer015]
  _GroupVersion = 1
COMPONENT P9 — geometry summary ("SupportDroite120d"; no construction recipe available for this part):
  bounding box: 22.0 x 20.7 x 15.2 mm
  tessellated surface: 2,312 triangles
  volume: 1668 mm^3 (24% of its bounding box)
COMPONENT P10 — recipe-attached ("CoinBAU", modeled in this document).
Construction recipe (the document's own serialized feature program — sketch geometry with constraints, then the solid features built on it; lengths are millimeters unless a unit is written):

FEATURE [PartDesign::SubShapeBinder] Binder  label="Binder(Chamfer023)"
  BindCopyOnChange = 0
  BindMode = 0
  ClaimChildren = false
  Context = -> Part010 [Body030.Binder.]
  EdgeTolerance = 1e-06
  FillStyle = 0
  Fuse = false
  InvalidShape = false
  MakeFace = true
  MergeEdges = true
  OffsetFill = false
  OffsetIntersection = false
  OffsetJoinType = 0
  OffsetOpenResult = false
  Outline = false
  PartialLoad = false
  Refine = true
  Relative = true
  SplitEdges = false
  Support = -> [Chamfer023[Face30]]
  TightBound = false
  TreeRank = 0
  ValidateShape = true
  _Version = 8
FEATURE [Sketcher::SketchObject] Sketch067
  ArcFitTolerance = 0
  AttachmentSupport = -> [Binder]
  ExternalBSplineMaxDegree = 0
  ExternalBSplineTolerance = 0
  ExternalGeometry = -> [Binder]
  FullyConstrained = true
  InternalTolerance = 1e-06
  InvalidShape = false
  MakeInternals = false
  MapMode = 5
  Placement = pos=(-2.82e-14,-50.4105,60.0769) rot=(1,0,0;0.698132rad)
  Support = -> [Binder]
  TreeRank = 0
  ValidateShape = true
  sketch-geometry (3):
    g0: Circle CenterX=-2e-16 CenterY=-32.5627 CenterZ=0 NormalX=0 NormalY=0 NormalZ=1 AngleXU=0 Radius=8
    g1: Circle CenterX=14 CenterY=-14.7181 CenterZ=0 NormalX=0 NormalY=0 NormalZ=1 AngleXU=0 Radius=1.6
    g2: Circle CenterX=-14 CenterY=-14.7181 CenterZ=0 NormalX=0 NormalY=0 NormalZ=1 AngleXU=0 Radius=1.6
  constraints (6):
    c: Coincident(g0,g-9)
    c: Diameter(g0) = 16
    c: Coincident(g1,g-10)
    c: Coincident(g2,g-11)
    c: Diameter(g2) = 3.2
    c: Equal(g2,g1)
FEATURE [PartDesign::Pad] Pad035
  AddSubType = 0
  AutoTaperInnerAngle = false
  CheckUpToFaceLimits = true
  ClaimChildren = false
  Direction = (-4e-16,-0.642788,0.766044)
  Fit = 0
  FitJoin = 0
  InnerFit = 0
  InnerFitJoin = 0
  InvalidShape = false
  Length = 3
  Length2 = 100
  Linearize = true
  NewSolid = false
  Profile = -> Sketch067
  Refine = true
  Suppress = false
  TaperInnerAngle = 0
  TaperInnerAngleRev = 0
  TreeRank = 0
  Type = 0
  ValidateShape = true
  _ProfileBasedVersion = 1
FEATURE [PartDesign::Chamfer] Chamfer021
  AddSubType = 0
  Angle = 45
  Base = -> Pad035 [Edge8,Edge11,Edge5,Edge1,Edge14,Edge2]
  BaseFeature = -> Pad035
  ChamferType = 0
  FlipDirection = false
  InvalidShape = false
  NewSolid = false
  Refine = true
  Size = 0.4
  Size2 = 1
  SupportTransform = false
  Suppress = false
  TreeRank = 0
  ValidateShape = true
FEATURE [PartDesign::Body] Body030  label="PlateBAU"
  AutoGroupSolids = false
  ClaimAllChildren = false
  ExportMode = 0
  Group = -> [Binder,Sketch067,Pad035,Chamfer021]
  InvalidShape = false
  Origin = -> Origin048
  SingleSolid = true
  Tip = -> Chamfer021
  TreeRank = 0
  ValidateShape = true
  _ExportChildren = -> [Binder,Pad035,Chamfer021]
  _GroupVersion = 1
